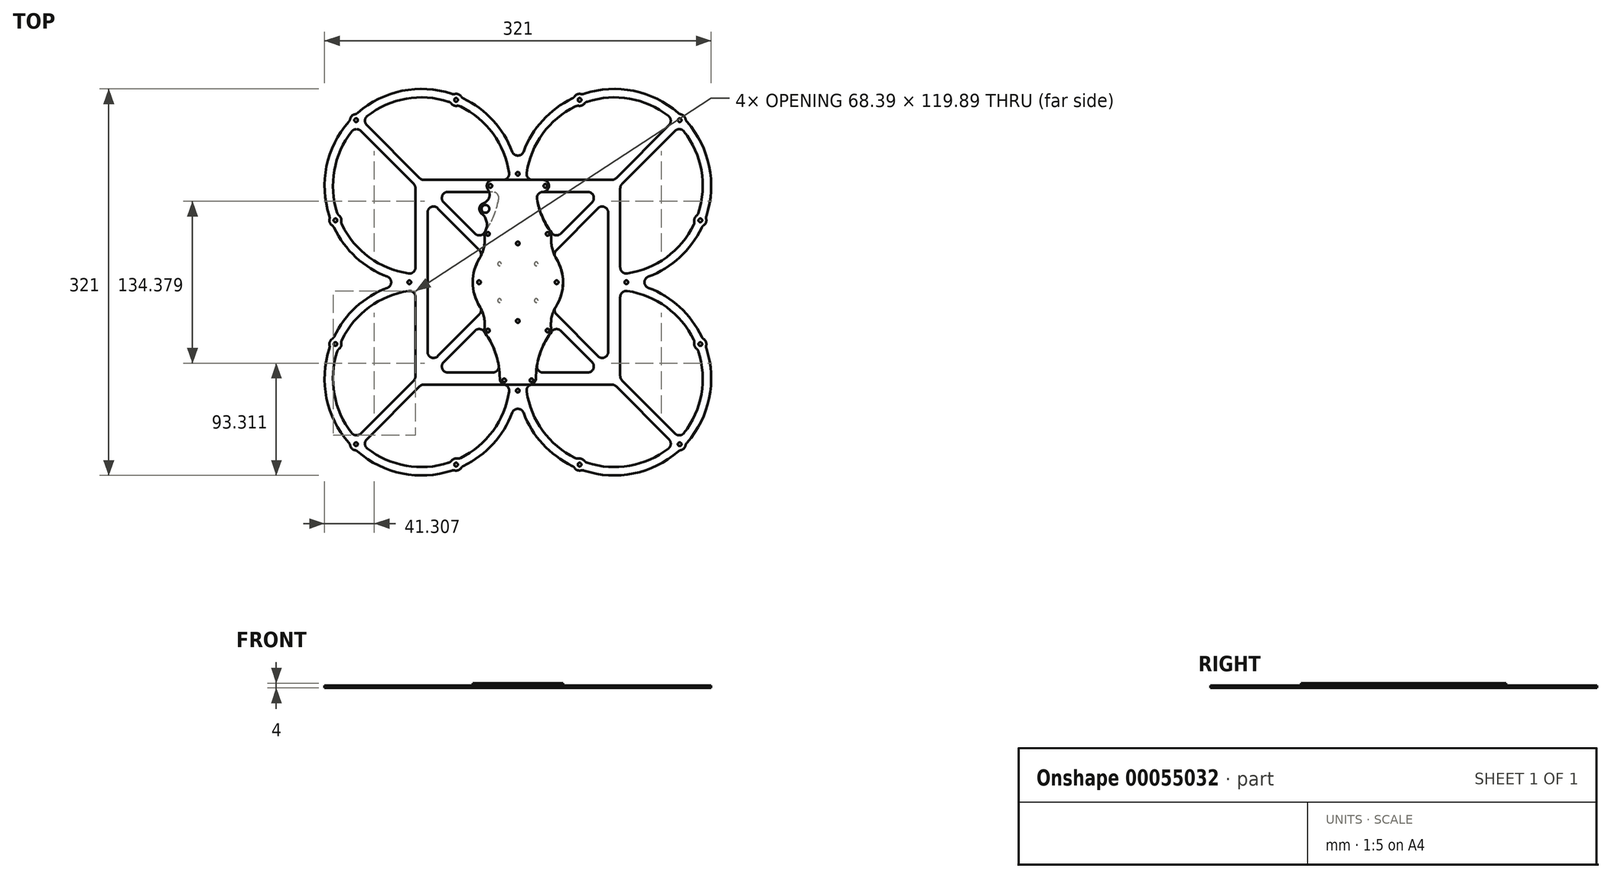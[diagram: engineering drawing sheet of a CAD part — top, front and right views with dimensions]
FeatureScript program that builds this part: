
annotation { "Feature Type Name" : "Feature", "Feature Type Description" : "" }
export const myFeature = defineFeature(function(context is Context, id is Id, definition is map)
    precondition{}
    {
        {
            var Q0;
            Q0=qCreatedBy(makeId("Top.planeOp"),FACE);
            var sketch = newSketch(context, id + "F0", { "sketchPlane" : qUnion([Q0])});
            skPoint(sketch, "E0.rect.middle", {"position": v(0, 0) * mm});
            skArc(sketch, "E1", {"start": v(80, -66) * mm, "mid": v(79.97, -66) * mm, "end": v(79.94, -66) * mm});
            skLineSegment(sketch, "E2.rect.bottom", {"start": v(15.25, -15.25) * mm, "end": v(-15.25, -15.25) * mm, "construction": true});
            skLineSegment(sketch, "E2.rect.top", {"start": v(15.25, 15.25) * mm, "end": v(-15.25, 15.25) * mm, "construction": true});
            skLineSegment(sketch, "E2.rect.left", {"start": v(15.25, -15.25) * mm, "end": v(15.25, 15.25) * mm, "construction": true});
            skLineSegment(sketch, "E2.rect.right", {"start": v(-15.25, -15.25) * mm, "end": v(-15.25, 15.25) * mm, "construction": true});
            skCircle(sketch, "E3", {"center": v(-80, 80) * mm, "radius": 63.5 * mm, "construction": true});
            skCircle(sketch, "E4", {"center": v(80, 80) * mm, "radius": 63.5 * mm, "construction": true});
            skCircle(sketch, "E5", {"center": v(-80, -80) * mm, "radius": 63.5 * mm, "construction": true});
            skCircle(sketch, "E6", {"center": v(80, -80) * mm, "radius": 63.5 * mm, "construction": true});
            skLineSegment(sketch, "E7.rect.bottom", {"start": v(26, -26) * mm, "end": v(-26, -26) * mm});
            skLineSegment(sketch, "E7.rect.top", {"start": v(26, 26) * mm, "end": v(-26, 26) * mm});
            skLineSegment(sketch, "E7.rect.left", {"start": v(26, -26) * mm, "end": v(26, 26) * mm});
            skLineSegment(sketch, "E7.rect.right", {"start": v(-26, -26) * mm, "end": v(-26, 26) * mm});
            skLineSegment(sketch, "E8.0", {"start": v(-85, -63.84) * mm, "end": v(-85, -12.23) * mm});
            skLineSegment(sketch, "E8.1", {"start": v(63.84, -85) * mm, "end": v(12.23, -85) * mm});
            skLineSegment(sketch, "E8.2", {"start": v(85, -63.84) * mm, "end": v(85, -12.23) * mm});
            skLineSegment(sketch, "E8.3", {"start": v(63.84, 85) * mm, "end": v(12.23, 85) * mm});
            skLineSegment(sketch, "E9.0", {"start": v(51.3, 75) * mm, "end": v(20.84, 75) * mm});
            skLineSegment(sketch, "E9.1", {"start": v(75, -51.34) * mm, "end": v(75, 51.3) * mm});
            skLineSegment(sketch, "E9.2", {"start": v(51.3, -75) * mm, "end": v(20.84, -75) * mm});
            skLineSegment(sketch, "E9.3", {"start": v(-75, -51.3) * mm, "end": v(-75, 51.3) * mm});
            skPoint(sketch, "E10", {"position": v(0, -124.8) * mm});
            skPoint(sketch, "E11.orphan", {"position": v(0, 114.1) * mm});
            skLineSegment(sketch, "E12.trimOffspring", {"start": v(-85, 12.23) * mm, "end": v(-85, 63.84) * mm});
            skLineSegment(sketch, "E13.trimOffspring", {"start": v(85, 12.23) * mm, "end": v(85, 63.84) * mm});
            skLineSegment(sketch, "E14.trimOffspring", {"start": v(-12.23, -85) * mm, "end": v(-63.84, -85) * mm});
            skLineSegment(sketch, "E15.trimOffspring", {"start": v(-12.23, 85) * mm, "end": v(-63.84, 85) * mm});
            skLineSegment(sketch, "E16", {"start": v(-124.66, 124.8) * mm, "end": v(-125, 125.15) * mm, "construction": true});
            skLineSegment(sketch, "E17", {"start": v(124.66, 124.8) * mm, "end": v(124.83, 124.97) * mm, "construction": true});
            skLineSegment(sketch, "E18", {"start": v(124.66, -124.8) * mm, "end": v(124.83, -124.97) * mm, "construction": true});
            skLineSegment(sketch, "E19", {"start": v(-124.66, -124.8) * mm, "end": v(-124.83, -124.97) * mm, "construction": true});
            skLineSegment(sketch, "E20.0", {"start": v(-94.48, 89.54) * mm, "end": v(-130.46, 125.67) * mm});
            skLineSegment(sketch, "E21.0", {"start": v(94.48, 89.54) * mm, "end": v(130.46, 125.67) * mm});
            skLineSegment(sketch, "E22.0", {"start": v(89.54, -94.5) * mm, "end": v(125.5, -130.61) * mm});
            skLineSegment(sketch, "E23.0", {"start": v(-94.48, -89.54) * mm, "end": v(-130.46, -125.67) * mm});
            skLineSegment(sketch, "E24.0", {"start": v(-89.54, 94.5) * mm, "end": v(-125.5, 130.61) * mm});
            skLineSegment(sketch, "E25.0", {"start": v(89.54, 94.5) * mm, "end": v(125.5, 130.61) * mm});
            skLineSegment(sketch, "E26.0", {"start": v(94.48, -89.54) * mm, "end": v(130.46, -125.67) * mm});
            skLineSegment(sketch, "E27.0", {"start": v(-89.54, -94.5) * mm, "end": v(-125.5, -130.61) * mm});
            skPoint(sketch, "E28.orphan", {"position": v(-89.9, 89.9) * mm});
            skPoint(sketch, "E29.orphan", {"position": v(-133.3, 133.48) * mm});
            skPoint(sketch, "E30.orphan", {"position": v(89.9, 89.9) * mm});
            skPoint(sketch, "E31.orphan", {"position": v(131.88, 132.06) * mm});
            skPoint(sketch, "E32.orphan", {"position": v(89.9, -89.9) * mm});
            skPoint(sketch, "E33.orphan", {"position": v(131.88, -132.06) * mm});
            skPoint(sketch, "E34.orphan", {"position": v(-89.9, -89.9) * mm});
            skPoint(sketch, "E35.orphan", {"position": v(-131.88, -132.06) * mm});
            skLineSegment(sketch, "E36", {"start": v(-87.42, 92.37) * mm, "end": v(-87.11, 92.06) * mm});
            skLineSegment(sketch, "E37", {"start": v(-92.38, 87.43) * mm, "end": v(-92.06, 87.1) * mm});
            skLineSegment(sketch, "E38", {"start": v(87.42, 92.37) * mm, "end": v(87.11, 92.06) * mm});
            skLineSegment(sketch, "E39", {"start": v(92.38, 87.43) * mm, "end": v(92.06, 87.1) * mm});
            skLineSegment(sketch, "E40", {"start": v(92.38, -87.43) * mm, "end": v(92.06, -87.1) * mm});
            skLineSegment(sketch, "E41", {"start": v(87.42, -92.37) * mm, "end": v(87.11, -92.06) * mm});
            skLineSegment(sketch, "E42", {"start": v(-92.38, -87.43) * mm, "end": v(-92.06, -87.1) * mm});
            skLineSegment(sketch, "E43", {"start": v(-87.42, -92.37) * mm, "end": v(-87.11, -92.06) * mm});
            skPoint(sketch, "E44.visualSharp", {"position": v(-66.92, 85) * mm});
            skPoint(sketch, "E45.visualSharp", {"position": v(-85, 66.92) * mm});
            skPoint(sketch, "E46.visualSharp", {"position": v(-61.92, 75) * mm});
            skPoint(sketch, "E47.visualSharp", {"position": v(-75, 61.92) * mm});
            skArc(sketch, "E48.filletArc", {"start": v(-125.02, 138.1) * mm, "mid": v(-126.95, 134.46) * mm, "end": v(-125.5, 130.61) * mm});
            skArc(sketch, "E49.filletArc", {"start": v(-130.46, 125.67) * mm, "mid": v(-134.3, 127.13) * mm, "end": v(-137.94, 125.22) * mm});
            skPoint(sketch, "E50.visualSharp", {"position": v(-4.93, 114.55) * mm});
            skPoint(sketch, "E51.visualSharp", {"position": v(5, 114.56) * mm});
            skPoint(sketch, "E52.visualSharp", {"position": v(66.92, 85) * mm});
            skArc(sketch, "E53.filletArc", {"start": v(125.5, 130.61) * mm, "mid": v(126.95, 134.46) * mm, "end": v(125.02, 138.1) * mm});
            skArc(sketch, "E54.filletArc", {"start": v(137.94, 125.22) * mm, "mid": v(134.3, 127.13) * mm, "end": v(130.46, 125.67) * mm});
            skPoint(sketch, "E55.visualSharp", {"position": v(85, 66.92) * mm});
            skPoint(sketch, "E56.visualSharp", {"position": v(61.92, 75) * mm});
            skPoint(sketch, "E57.visualSharp", {"position": v(75, 61.92) * mm});
            skLineSegment(sketch, "E57.filletArc", {"start": v(75, 51.3) * mm, "end": v(75, 51.3) * mm});
            skPoint(sketch, "E58.visualSharp", {"position": v(85, -66.92) * mm});
            skArc(sketch, "E59.filletArc", {"start": v(130.46, -125.67) * mm, "mid": v(134.3, -127.13) * mm, "end": v(137.94, -125.22) * mm});
            skArc(sketch, "E60.filletArc", {"start": v(125.02, -138.1) * mm, "mid": v(126.95, -134.46) * mm, "end": v(125.5, -130.61) * mm});
            skPoint(sketch, "E61.visualSharp", {"position": v(66.92, -85) * mm});
            skPoint(sketch, "E62.visualSharp", {"position": v(61.92, -75) * mm});
            skPoint(sketch, "E63.visualSharp", {"position": v(75, -61.96) * mm});
            skPoint(sketch, "E64.visualSharp", {"position": v(-5.02, -114.56) * mm});
            skPoint(sketch, "E65.visualSharp", {"position": v(-66.92, -85) * mm});
            skArc(sketch, "E66.filletArc", {"start": v(-125.5, -130.61) * mm, "mid": v(-126.95, -134.46) * mm, "end": v(-125.02, -138.1) * mm});
            skArc(sketch, "E67.filletArc", {"start": v(-137.94, -125.22) * mm, "mid": v(-134.3, -127.13) * mm, "end": v(-130.46, -125.67) * mm});
            skPoint(sketch, "E68.visualSharp", {"position": v(-85, -66.92) * mm});
            skPoint(sketch, "E69.visualSharp", {"position": v(-61.92, -75) * mm});
            skPoint(sketch, "E70.visualSharp", {"position": v(-75, -61.92) * mm});
            skArc(sketch, "E71", {"start": v(33.54, -16.78) * mm, "mid": v(37.5, 0) * mm, "end": v(33.54, 16.77) * mm});
            skArc(sketch, "E72.trimOffspring", {"start": v(-33.54, 16.77) * mm, "mid": v(-37.5, 0) * mm, "end": v(-33.54, -16.77) * mm});
            skPoint(sketch, "E73.visualSharp", {"position": v(-19.22, 32.2) * mm});
            skPoint(sketch, "E74.visualSharp", {"position": v(19.22, 32.2) * mm});
            skPoint(sketch, "E75.visualSharp", {"position": v(32.2, 19.22) * mm});
            skPoint(sketch, "E76.visualSharp", {"position": v(32.2, -19.23) * mm});
            skPoint(sketch, "E77.visualSharp", {"position": v(-32.2, -19.22) * mm});
            skPoint(sketch, "E78.visualSharp", {"position": v(-32.2, 19.22) * mm});
            skCircle(sketch, "E79", {"center": v(15.25, -15.25) * mm, "radius": 1.5 * mm});
            skCircle(sketch, "E80", {"center": v(-15.25, -15.25) * mm, "radius": 1.5 * mm});
            skCircle(sketch, "E81", {"center": v(-15.25, 15.25) * mm, "radius": 1.5 * mm});
            skCircle(sketch, "E82", {"center": v(15.25, 15.25) * mm, "radius": 1.5 * mm});
            skCircle(sketch, "E83", {"center": v(32.2, 0) * mm, "radius": 1.5 * mm});
            skCircle(sketch, "E84", {"center": v(0, -32.2) * mm, "radius": 1.5 * mm});
            skLineSegment(sketch, "E85", {"start": v(0, -141.51) * mm, "end": v(0, 75) * mm, "construction": true});
            skLineSegment(sketch, "E86", {"start": v(141.95, 0) * mm, "end": v(-75, 0) * mm, "construction": true});
            skCircle(sketch, "E87.MirrorC", {"center": v(-32.2, 0) * mm, "radius": 1.5 * mm});
            skCircle(sketch, "E88.MirrorC", {"center": v(0, 32.2) * mm, "radius": 1.5 * mm});
            skArc(sketch, "E89.filletArc", {"start": v(12.23, -85) * mm, "mid": v(8.45, -86.73) * mm, "end": v(7.29, -90.73) * mm});
            skArc(sketch, "E90.filletArc", {"start": v(-7.29, -90.73) * mm, "mid": v(-8.45, -86.73) * mm, "end": v(-12.23, -85) * mm});
            skArc(sketch, "E91.filletArc", {"start": v(4.68, -108.4) * mm, "mid": v(0, -105.17) * mm, "end": v(-4.68, -108.4) * mm});
            skPoint(sketch, "E92.visualSharp", {"position": v(6.67, 85) * mm});
            skArc(sketch, "E92.filletArc", {"start": v(7.29, 90.73) * mm, "mid": v(8.45, 86.73) * mm, "end": v(12.23, 85) * mm});
            skPoint(sketch, "E93.visualSharp", {"position": v(-6.67, 85) * mm});
            skArc(sketch, "E93.filletArc", {"start": v(-12.23, 85) * mm, "mid": v(-8.45, 86.73) * mm, "end": v(-7.29, 90.73) * mm});
            skPoint(sketch, "E94.visualSharp", {"position": v(0, 88.96) * mm});
            skArc(sketch, "E94.filletArc", {"start": v(-4.68, 108.4) * mm, "mid": v(0, 105.17) * mm, "end": v(4.68, 108.4) * mm});
            skArc(sketch, "E95.filletArc", {"start": v(-85, -12.23) * mm, "mid": v(-86.73, -8.45) * mm, "end": v(-90.73, -7.29) * mm});
            skArc(sketch, "E96.filletArc", {"start": v(-90.73, 7.29) * mm, "mid": v(-86.73, 8.45) * mm, "end": v(-85, 12.23) * mm});
            skPoint(sketch, "E97.visualSharp", {"position": v(-88.96, 0) * mm});
            skArc(sketch, "E97.filletArc", {"start": v(-108.4, -4.68) * mm, "mid": v(-105.17, 0) * mm, "end": v(-108.4, 4.68) * mm});
            skPoint(sketch, "E98.visualSharp", {"position": v(85, -6.67) * mm});
            skArc(sketch, "E98.filletArc", {"start": v(90.73, -7.29) * mm, "mid": v(86.73, -8.45) * mm, "end": v(85, -12.23) * mm});
            skPoint(sketch, "E99.visualSharp", {"position": v(85, 6.67) * mm});
            skArc(sketch, "E99.filletArc", {"start": v(85, 12.23) * mm, "mid": v(86.73, 8.45) * mm, "end": v(90.73, 7.29) * mm});
            skArc(sketch, "E100.filletArc", {"start": v(108.4, 4.68) * mm, "mid": v(105.17, 0) * mm, "end": v(108.4, -4.68) * mm});
            skArc(sketch, "E101", {"start": v(-90.73, 7.29) * mm, "mid": v(-123.42, 20.7) * mm, "end": v(-146.07, 47.8) * mm});
            skArc(sketch, "E102", {"start": v(-108.4, 4.68) * mm, "mid": v(-134.45, 20.7) * mm, "end": v(-152.63, 45.3) * mm});
            skArc(sketch, "E103", {"start": v(-7.29, 90.73) * mm, "mid": v(-20.66, 123.37) * mm, "end": v(-47.7, 146.02) * mm});
            skLineSegment(sketch, "E104", {"start": v(-138.95, 56.4) * mm, "end": v(-148.23, 52.68) * mm, "construction": true});
            skLineSegment(sketch, "E105", {"start": v(-148.23, 52.68) * mm, "end": v(-160.6, 47.73) * mm, "construction": true});
            skLineSegment(sketch, "E106", {"start": v(-52.57, 148.19) * mm, "end": v(-48.09, 159.32) * mm, "construction": true});
            skCircle(sketch, "E107", {"center": v(-80, 80) * mm, "radius": 77 * mm, "construction": true});
            skArc(sketch, "E108", {"start": v(-156.38, 52.4) * mm, "mid": v(-156.13, 49.52) * mm, "end": v(-154.31, 47.26) * mm});
            skArc(sketch, "E109", {"start": v(-55.18, 148.34) * mm, "mid": v(-53.13, 146.8) * mm, "end": v(-50.58, 146.48) * mm});
            skArc(sketch, "E110.trimOffspring", {"start": v(-47.14, 154.26) * mm, "mid": v(-49.4, 156.07) * mm, "end": v(-52.28, 156.33) * mm});
            skArc(sketch, "E111.trimOffspring", {"start": v(-45.17, 152.58) * mm, "mid": v(-20.66, 134.4) * mm, "end": v(-4.68, 108.4) * mm});
            skArc(sketch, "E112.trimOffspring", {"start": v(-57.58, 150) * mm, "mid": v(-92.77, 152.38) * mm, "end": v(-125.02, 138.1) * mm});
            skPoint(sketch, "E113.visualSharp", {"position": v(-46.6, 153.24) * mm});
            skArc(sketch, "E113.filletArc", {"start": v(-47.14, 154.26) * mm, "mid": v(-46.26, 153.29) * mm, "end": v(-45.17, 152.58) * mm});
            skPoint(sketch, "E114.visualSharp", {"position": v(-49.36, 146.81) * mm});
            skArc(sketch, "E114.filletArc", {"start": v(-47.7, 146.02) * mm, "mid": v(-49.1, 146.47) * mm, "end": v(-50.58, 146.48) * mm});
            skPoint(sketch, "E115.visualSharp", {"position": v(-55.83, 149.41) * mm});
            skArc(sketch, "E115.filletArc", {"start": v(-55.18, 148.34) * mm, "mid": v(-56.26, 149.35) * mm, "end": v(-57.58, 150) * mm});
            skPoint(sketch, "E116.visualSharp", {"position": v(-53.37, 155.97) * mm});
            skArc(sketch, "E116.filletArc", {"start": v(-54.86, 156.48) * mm, "mid": v(-53.58, 156.23) * mm, "end": v(-52.28, 156.33) * mm});
            skArc(sketch, "E117.trimOffspring", {"start": v(-156.52, 55) * mm, "mid": v(-158.84, 96.26) * mm, "end": v(-140.38, 133.24) * mm});
            skArc(sketch, "E118.trimOffspring", {"start": v(-150.04, 57.7) * mm, "mid": v(-152.35, 92.96) * mm, "end": v(-137.94, 125.22) * mm});
            skArc(sketch, "E119.trimOffspring", {"start": v(-146.53, 50.69) * mm, "mid": v(-146.84, 53.24) * mm, "end": v(-148.38, 55.3) * mm});
            skPoint(sketch, "E120.visualSharp", {"position": v(-153.3, 46.72) * mm});
            skArc(sketch, "E120.filletArc", {"start": v(-152.63, 45.3) * mm, "mid": v(-153.35, 46.39) * mm, "end": v(-154.31, 47.26) * mm});
            skPoint(sketch, "E121.visualSharp", {"position": v(-146.86, 49.47) * mm});
            skArc(sketch, "E121.filletArc", {"start": v(-146.53, 50.69) * mm, "mid": v(-146.52, 49.21) * mm, "end": v(-146.07, 47.8) * mm});
            skPoint(sketch, "E122.visualSharp", {"position": v(-149.45, 55.95) * mm});
            skArc(sketch, "E122.filletArc", {"start": v(-150.04, 57.7) * mm, "mid": v(-149.39, 56.38) * mm, "end": v(-148.38, 55.3) * mm});
            skPoint(sketch, "E123.visualSharp", {"position": v(-156.01, 53.5) * mm});
            skArc(sketch, "E123.filletArc", {"start": v(-156.38, 52.4) * mm, "mid": v(-156.28, 53.71) * mm, "end": v(-156.52, 55) * mm});
            skCircle(sketch, "E124", {"center": v(-151.48, 51.38) * mm, "radius": 1.5 * mm});
            skCircle(sketch, "E125", {"center": v(-51.26, 151.44) * mm, "radius": 1.5 * mm});
            skArc(sketch, "E126", {"start": v(7.29, 90.73) * mm, "mid": v(20.66, 123.37) * mm, "end": v(47.7, 146.02) * mm});
            skArc(sketch, "E127", {"start": v(137.94, 125.22) * mm, "mid": v(152.35, 92.96) * mm, "end": v(150.04, 57.7) * mm});
            skArc(sketch, "E128", {"start": v(4.68, 108.4) * mm, "mid": v(20.66, 134.4) * mm, "end": v(45.17, 152.58) * mm});
            skArc(sketch, "E129", {"start": v(90.73, -7.29) * mm, "mid": v(123.42, -20.7) * mm, "end": v(146.07, -47.8) * mm});
            skArc(sketch, "E130", {"start": v(125.02, -138.1) * mm, "mid": v(92.77, -152.38) * mm, "end": v(57.58, -150) * mm});
            skArc(sketch, "E131", {"start": v(108.4, -4.68) * mm, "mid": v(134.45, -20.7) * mm, "end": v(152.63, -45.3) * mm});
            skArc(sketch, "E132", {"start": v(-90.73, -7.29) * mm, "mid": v(-123.42, -20.7) * mm, "end": v(-146.07, -47.8) * mm});
            skArc(sketch, "E133", {"start": v(-125.02, -138.1) * mm, "mid": v(-92.77, -152.38) * mm, "end": v(-57.58, -150) * mm});
            skArc(sketch, "E134", {"start": v(-108.4, -4.68) * mm, "mid": v(-134.45, -20.7) * mm, "end": v(-152.63, -45.3) * mm});
            skArc(sketch, "E135.MirrorCS", {"start": v(47.14, 154.26) * mm, "mid": v(49.4, 156.07) * mm, "end": v(52.28, 156.33) * mm});
            skArc(sketch, "E136.MirrorCS", {"start": v(55.18, 148.34) * mm, "mid": v(53.13, 146.8) * mm, "end": v(50.58, 146.48) * mm});
            skCircle(sketch, "E137.MirrorC", {"center": v(51.26, 151.44) * mm, "radius": 1.5 * mm});
            skArc(sketch, "E138.MirrorCS", {"start": v(55.18, 148.34) * mm, "mid": v(56.26, 149.35) * mm, "end": v(57.58, 150) * mm});
            skArc(sketch, "E139.MirrorCS", {"start": v(47.7, 146.02) * mm, "mid": v(49.1, 146.47) * mm, "end": v(50.58, 146.48) * mm});
            skArc(sketch, "E140.MirrorCS", {"start": v(47.14, 154.26) * mm, "mid": v(46.26, 153.29) * mm, "end": v(45.17, 152.58) * mm});
            skArc(sketch, "E141.MirrorCS", {"start": v(54.86, 156.48) * mm, "mid": v(53.58, 156.23) * mm, "end": v(52.28, 156.33) * mm});
            skCircle(sketch, "E142.MirrorC", {"center": v(151.48, 51.38) * mm, "radius": 1.5 * mm});
            skArc(sketch, "E143.MirrorCS", {"start": v(146.53, 50.69) * mm, "mid": v(146.84, 53.24) * mm, "end": v(148.38, 55.3) * mm});
            skArc(sketch, "E144.MirrorCS", {"start": v(156.38, 52.4) * mm, "mid": v(156.13, 49.52) * mm, "end": v(154.31, 47.26) * mm});
            skArc(sketch, "E145.MirrorCS", {"start": v(156.38, 52.4) * mm, "mid": v(156.28, 53.71) * mm, "end": v(156.52, 55) * mm});
            skArc(sketch, "E146.MirrorCS", {"start": v(150.04, 57.7) * mm, "mid": v(149.39, 56.38) * mm, "end": v(148.38, 55.3) * mm});
            skArc(sketch, "E147.MirrorCS", {"start": v(146.53, 50.69) * mm, "mid": v(146.52, 49.21) * mm, "end": v(146.07, 47.8) * mm});
            skArc(sketch, "E148.MirrorCS", {"start": v(152.63, 45.3) * mm, "mid": v(153.35, 46.39) * mm, "end": v(154.31, 47.26) * mm});
            skLineSegment(sketch, "E149", {"start": v(-80, 80) * mm, "end": v(-139.42, 139.67) * mm, "construction": true});
            skArc(sketch, "E150", {"start": v(-135.3, 139.47) * mm, "mid": v(-137.86, 138.1) * mm, "end": v(-139.23, 135.55) * mm});
            skCircle(sketch, "E151", {"center": v(-134.33, 134.56) * mm, "radius": 1.5 * mm});
            skArc(sketch, "E152.trimOffspring", {"start": v(-132.98, 140.6) * mm, "mid": v(-96.03, 158.89) * mm, "end": v(-54.86, 156.48) * mm});
            skPoint(sketch, "E153.visualSharp", {"position": v(-139.33, 134.4) * mm});
            skArc(sketch, "E153.filletArc", {"start": v(-140.38, 133.24) * mm, "mid": v(-139.66, 134.32) * mm, "end": v(-139.23, 135.55) * mm});
            skPoint(sketch, "E154.visualSharp", {"position": v(-134.16, 139.56) * mm});
            skArc(sketch, "E154.filletArc", {"start": v(-135.3, 139.47) * mm, "mid": v(-134.07, 139.88) * mm, "end": v(-132.98, 140.6) * mm});
            skCircle(sketch, "E155.MirrorC", {"center": v(134.33, 134.56) * mm, "radius": 1.5 * mm});
            skArc(sketch, "E156.MirrorCS", {"start": v(135.3, 139.47) * mm, "mid": v(137.86, 138.1) * mm, "end": v(139.23, 135.55) * mm});
            skArc(sketch, "E157.MirrorCS", {"start": v(135.3, 139.47) * mm, "mid": v(134.07, 139.88) * mm, "end": v(132.98, 140.6) * mm});
            skArc(sketch, "E158.MirrorCS", {"start": v(140.38, 133.24) * mm, "mid": v(139.66, 134.32) * mm, "end": v(139.23, 135.55) * mm});
            skArc(sketch, "E159.trimOffspring", {"start": v(54.86, 156.48) * mm, "mid": v(96.03, 158.89) * mm, "end": v(132.98, 140.6) * mm});
            skArc(sketch, "E160.trimOffspring", {"start": v(57.58, 150) * mm, "mid": v(92.77, 152.38) * mm, "end": v(125.02, 138.1) * mm});
            skArc(sketch, "E161.trimOffspring", {"start": v(140.38, 133.24) * mm, "mid": v(158.84, 96.26) * mm, "end": v(156.52, 55) * mm});
            skArc(sketch, "E162.trimOffspring", {"start": v(146.07, 47.8) * mm, "mid": v(123.42, 20.7) * mm, "end": v(90.73, 7.29) * mm});
            skArc(sketch, "E163.trimOffspring", {"start": v(152.63, 45.3) * mm, "mid": v(134.45, 20.7) * mm, "end": v(108.4, 4.68) * mm});
            skArc(sketch, "E164.MirrorCS", {"start": v(-156.38, -52.4) * mm, "mid": v(-156.28, -53.71) * mm, "end": v(-156.52, -55) * mm});
            skArc(sketch, "E165.MirrorCS", {"start": v(-156.38, -52.4) * mm, "mid": v(-156.13, -49.52) * mm, "end": v(-154.31, -47.26) * mm});
            skArc(sketch, "E166.MirrorCS", {"start": v(-152.63, -45.3) * mm, "mid": v(-153.35, -46.39) * mm, "end": v(-154.31, -47.26) * mm});
            skArc(sketch, "E167.MirrorCS", {"start": v(-150.04, -57.7) * mm, "mid": v(-149.39, -56.38) * mm, "end": v(-148.38, -55.3) * mm});
            skArc(sketch, "E168.MirrorCS", {"start": v(-146.53, -50.69) * mm, "mid": v(-146.84, -53.24) * mm, "end": v(-148.38, -55.3) * mm});
            skArc(sketch, "E169.MirrorCS", {"start": v(-146.53, -50.69) * mm, "mid": v(-146.52, -49.21) * mm, "end": v(-146.07, -47.8) * mm});
            skArc(sketch, "E170.MirrorCS", {"start": v(-135.3, -139.47) * mm, "mid": v(-137.86, -138.1) * mm, "end": v(-139.23, -135.55) * mm});
            skArc(sketch, "E171.MirrorCS", {"start": v(-135.3, -139.47) * mm, "mid": v(-134.07, -139.88) * mm, "end": v(-132.98, -140.6) * mm});
            skArc(sketch, "E172.MirrorCS", {"start": v(-140.38, -133.24) * mm, "mid": v(-139.66, -134.32) * mm, "end": v(-139.23, -135.55) * mm});
            skArc(sketch, "E173.MirrorCS", {"start": v(-54.86, -156.48) * mm, "mid": v(-53.58, -156.23) * mm, "end": v(-52.28, -156.33) * mm});
            skArc(sketch, "E174.MirrorCS", {"start": v(-47.14, -154.26) * mm, "mid": v(-49.4, -156.07) * mm, "end": v(-52.28, -156.33) * mm});
            skArc(sketch, "E175.MirrorCS", {"start": v(-47.7, -146.02) * mm, "mid": v(-49.1, -146.47) * mm, "end": v(-50.58, -146.48) * mm});
            skArc(sketch, "E176.MirrorCS", {"start": v(-55.18, -148.34) * mm, "mid": v(-53.13, -146.8) * mm, "end": v(-50.58, -146.48) * mm});
            skArc(sketch, "E177.MirrorCS", {"start": v(-55.18, -148.34) * mm, "mid": v(-56.26, -149.35) * mm, "end": v(-57.58, -150) * mm});
            skArc(sketch, "E178.MirrorCS", {"start": v(47.14, -154.26) * mm, "mid": v(46.26, -153.29) * mm, "end": v(45.17, -152.58) * mm});
            skArc(sketch, "E179.MirrorCS", {"start": v(47.14, -154.26) * mm, "mid": v(49.4, -156.07) * mm, "end": v(52.28, -156.33) * mm});
            skArc(sketch, "E180.MirrorCS", {"start": v(54.86, -156.48) * mm, "mid": v(53.58, -156.23) * mm, "end": v(52.28, -156.33) * mm});
            skArc(sketch, "E181.MirrorCS", {"start": v(55.18, -148.34) * mm, "mid": v(56.26, -149.35) * mm, "end": v(57.58, -150) * mm});
            skArc(sketch, "E182.MirrorCS", {"start": v(55.18, -148.34) * mm, "mid": v(53.13, -146.8) * mm, "end": v(50.58, -146.48) * mm});
            skArc(sketch, "E183.MirrorCS", {"start": v(47.7, -146.02) * mm, "mid": v(49.1, -146.47) * mm, "end": v(50.58, -146.48) * mm});
            skCircle(sketch, "E184.MirrorC", {"center": v(51.26, -151.44) * mm, "radius": 1.5 * mm});
            skCircle(sketch, "E185.MirrorC", {"center": v(-51.26, -151.44) * mm, "radius": 1.5 * mm});
            skCircle(sketch, "E186.MirrorC", {"center": v(-134.33, -134.56) * mm, "radius": 1.5 * mm});
            skCircle(sketch, "E187.MirrorC", {"center": v(-151.48, -51.38) * mm, "radius": 1.5 * mm});
            skCircle(sketch, "E188.MirrorC", {"center": v(151.48, -51.38) * mm, "radius": 1.5 * mm});
            skArc(sketch, "E189.MirrorCS", {"start": v(150.04, -57.7) * mm, "mid": v(149.39, -56.38) * mm, "end": v(148.38, -55.3) * mm});
            skArc(sketch, "E190.MirrorCS", {"start": v(146.53, -50.69) * mm, "mid": v(146.84, -53.24) * mm, "end": v(148.38, -55.3) * mm});
            skArc(sketch, "E191.MirrorCS", {"start": v(146.53, -50.69) * mm, "mid": v(146.52, -49.21) * mm, "end": v(146.07, -47.8) * mm});
            skArc(sketch, "E192.MirrorCS", {"start": v(156.38, -52.4) * mm, "mid": v(156.28, -53.71) * mm, "end": v(156.52, -55) * mm});
            skArc(sketch, "E193.MirrorCS", {"start": v(156.38, -52.4) * mm, "mid": v(156.13, -49.52) * mm, "end": v(154.31, -47.26) * mm});
            skArc(sketch, "E194.MirrorCS", {"start": v(152.63, -45.3) * mm, "mid": v(153.35, -46.39) * mm, "end": v(154.31, -47.26) * mm});
            skCircle(sketch, "E195.MirrorC", {"center": v(134.33, -134.56) * mm, "radius": 1.5 * mm});
            skArc(sketch, "E196.MirrorCS", {"start": v(135.3, -139.47) * mm, "mid": v(134.07, -139.88) * mm, "end": v(132.98, -140.6) * mm});
            skArc(sketch, "E197.MirrorCS", {"start": v(135.3, -139.47) * mm, "mid": v(137.86, -138.1) * mm, "end": v(139.23, -135.55) * mm});
            skArc(sketch, "E198.MirrorCS", {"start": v(140.38, -133.24) * mm, "mid": v(139.66, -134.32) * mm, "end": v(139.23, -135.55) * mm});
            skArc(sketch, "E199.trimOffspring", {"start": v(150.04, -57.7) * mm, "mid": v(152.35, -92.96) * mm, "end": v(137.94, -125.22) * mm});
            skArc(sketch, "E200.trimOffspring", {"start": v(156.52, -55) * mm, "mid": v(158.84, -96.26) * mm, "end": v(140.38, -133.24) * mm});
            skArc(sketch, "E201.trimOffspring", {"start": v(132.98, -140.6) * mm, "mid": v(96.03, -158.89) * mm, "end": v(54.86, -156.48) * mm});
            skArc(sketch, "E202.trimOffspring", {"start": v(45.17, -152.58) * mm, "mid": v(20.66, -134.4) * mm, "end": v(4.68, -108.4) * mm});
            skArc(sketch, "E203.trimOffspring", {"start": v(47.7, -146.02) * mm, "mid": v(20.66, -123.37) * mm, "end": v(7.29, -90.73) * mm});
            skArc(sketch, "E204.trimOffspring", {"start": v(-47.7, -146.02) * mm, "mid": v(-20.66, -123.37) * mm, "end": v(-7.29, -90.73) * mm});
            skArc(sketch, "E205.MirrorCS", {"start": v(-47.14, -154.26) * mm, "mid": v(-46.26, -153.29) * mm, "end": v(-45.17, -152.58) * mm});
            skArc(sketch, "E206.trimOffspring", {"start": v(-45.17, -152.58) * mm, "mid": v(-20.66, -134.4) * mm, "end": v(-4.68, -108.4) * mm});
            skArc(sketch, "E207.trimOffspring", {"start": v(-132.98, -140.6) * mm, "mid": v(-96.03, -158.89) * mm, "end": v(-54.86, -156.48) * mm});
            skArc(sketch, "E208.trimOffspring", {"start": v(-156.52, -55) * mm, "mid": v(-158.84, -96.26) * mm, "end": v(-140.38, -133.24) * mm});
            skArc(sketch, "E209.trimOffspring", {"start": v(-150.04, -57.7) * mm, "mid": v(-152.35, -92.96) * mm, "end": v(-137.94, -125.22) * mm});
            skLineSegment(sketch, "E210.trimOffspring", {"start": v(-75, 0) * mm, "end": v(141.95, 0) * mm, "construction": true});
            skPoint(sketch, "E211.MirrorCS.start.orphan", {"position": v(-141.95, 0) * mm});
            skLineSegment(sketch, "E212.trimOffspring", {"start": v(-105.17, 0) * mm, "end": v(-110.17, 0) * mm, "construction": true});
            skCircle(sketch, "E213", {"center": v(-90.09, 0) * mm, "radius": 1.5 * mm});
            skLineSegment(sketch, "E214.trimOffspring", {"start": v(0, 105.17) * mm, "end": v(0, 141.51) * mm, "construction": true});
            skCircle(sketch, "E215", {"center": v(0, 90.09) * mm, "radius": 1.5 * mm});
            skCircle(sketch, "E216.MirrorC", {"center": v(0, -90.09) * mm, "radius": 1.5 * mm});
            skCircle(sketch, "E217.MirrorC", {"center": v(90.09, 0) * mm, "radius": 1.5 * mm});
            skLineSegment(sketch, "E218.trimOffspring", {"start": v(-56.3, 138.91) * mm, "end": v(-52.57, 148.19) * mm, "construction": true});
            skArc(sketch, "E219", {"start": v(-31.37, 20.54) * mm, "mid": v(-37.5, 0) * mm, "end": v(-31.37, -20.54) * mm});
            skLineSegment(sketch, "E220", {"start": v(89.54, 94.5) * mm, "end": v(81.55, 86.47) * mm});
            skLineSegment(sketch, "E221", {"start": v(94.48, 89.54) * mm, "end": v(86.46, 81.48) * mm});
            skLineSegment(sketch, "E222", {"start": v(63.84, 85) * mm, "end": v(78, 85) * mm});
            skLineSegment(sketch, "E223", {"start": v(51.3, 75) * mm, "end": v(58.09, 75) * mm});
            skLineSegment(sketch, "E224", {"start": v(85, 63.84) * mm, "end": v(85, 77.95) * mm});
            skLineSegment(sketch, "E225", {"start": v(75, 51.3) * mm, "end": v(75, 57.87) * mm});
            skLineSegment(sketch, "E226", {"start": v(-89.54, 94.5) * mm, "end": v(-81.55, 86.47) * mm});
            skLineSegment(sketch, "E227", {"start": v(-94.48, 89.54) * mm, "end": v(-86.46, 81.48) * mm});
            skLineSegment(sketch, "E228", {"start": v(-63.84, 85) * mm, "end": v(-78, 85) * mm});
            skLineSegment(sketch, "E229", {"start": v(-51.3, 75) * mm, "end": v(-58.09, 75) * mm});
            skLineSegment(sketch, "E230", {"start": v(-75, 51.3) * mm, "end": v(-75, 57.87) * mm});
            skLineSegment(sketch, "E231", {"start": v(-85, 63.84) * mm, "end": v(-85, 77.95) * mm});
            skPoint(sketch, "E232.1.internal.orphan", {"position": v(-26, 0) * mm});
            skPoint(sketch, "E233.1.internal.orphan", {"position": v(0, 26) * mm});
            skArc(sketch, "E234", {"start": v(-15.9, 69.17) * mm, "mid": v(-20.3, 54.3) * mm, "end": v(-28.1, 40.88) * mm});
            skArc(sketch, "E235", {"start": v(15.9, 69.17) * mm, "mid": v(20.3, 54.3) * mm, "end": v(28.1, 40.88) * mm});
            skLineSegment(sketch, "E236", {"start": v(94.48, -89.54) * mm, "end": v(86.46, -81.48) * mm});
            skLineSegment(sketch, "E237", {"start": v(89.54, -94.5) * mm, "end": v(81.55, -86.47) * mm});
            skLineSegment(sketch, "E238", {"start": v(75, -51.34) * mm, "end": v(75, -57.87) * mm});
            skLineSegment(sketch, "E239", {"start": v(51.3, -75) * mm, "end": v(58.09, -75) * mm});
            skLineSegment(sketch, "E240", {"start": v(63.84, -85) * mm, "end": v(78, -85) * mm});
            skLineSegment(sketch, "E241", {"start": v(85, -63.84) * mm, "end": v(85, -77.95) * mm});
            skPoint(sketch, "E242.1.internal.orphan", {"position": v(26, 0) * mm});
            skLineSegment(sketch, "E243", {"start": v(-94.48, -89.54) * mm, "end": v(-86.46, -81.48) * mm});
            skLineSegment(sketch, "E244", {"start": v(-89.54, -94.5) * mm, "end": v(-81.55, -86.47) * mm});
            skLineSegment(sketch, "E245", {"start": v(-85, -63.84) * mm, "end": v(-85, -77.95) * mm});
            skLineSegment(sketch, "E246", {"start": v(-63.84, -85) * mm, "end": v(-78, -85) * mm});
            skLineSegment(sketch, "E247", {"start": v(-51.3, -75) * mm, "end": v(-58.09, -75) * mm});
            skLineSegment(sketch, "E248", {"start": v(-75, -51.3) * mm, "end": v(-75, -57.87) * mm});
            skPoint(sketch, "E249.1.internal.orphan", {"position": v(0, -26) * mm});
            skArc(sketch, "E250", {"start": v(28.1, -40.88) * mm, "mid": v(20.3, -54.3) * mm, "end": v(15.9, -69.17) * mm});
            skArc(sketch, "E251", {"start": v(-28.1, -40.88) * mm, "mid": v(-20.3, -54.3) * mm, "end": v(-15.9, -69.17) * mm});
            skLineSegment(sketch, "E252.trimOffspring", {"start": v(-61.63, 66.47) * mm, "end": v(-35.63, 40.36) * mm});
            skLineSegment(sketch, "E253.trimOffspring", {"start": v(-66.46, 61.4) * mm, "end": v(-32.01, 26.8) * mm});
            skLineSegment(sketch, "E254.trimOffspring", {"start": v(61.63, 66.47) * mm, "end": v(35.63, 40.36) * mm});
            skLineSegment(sketch, "E255.trimOffspring", {"start": v(66.46, 61.4) * mm, "end": v(32.01, 26.8) * mm});
            skLineSegment(sketch, "E256.trimOffspring", {"start": v(66.46, -61.4) * mm, "end": v(32.01, -26.8) * mm});
            skLineSegment(sketch, "E257.trimOffspring", {"start": v(61.63, -66.47) * mm, "end": v(35.63, -40.36) * mm});
            skLineSegment(sketch, "E258.trimOffspring", {"start": v(-61.63, -66.47) * mm, "end": v(-35.63, -40.36) * mm});
            skLineSegment(sketch, "E259.trimOffspring", {"start": v(-66.46, -61.4) * mm, "end": v(-32.01, -26.8) * mm});
            skPoint(sketch, "E260.visualSharp", {"position": v(-70.12, 75) * mm});
            skArc(sketch, "E260.filletArc", {"start": v(-58.09, 75) * mm, "mid": v(-62.7, 71.92) * mm, "end": v(-61.63, 66.47) * mm});
            skPoint(sketch, "E261.visualSharp", {"position": v(-75, 69.98) * mm});
            skArc(sketch, "E261.filletArc", {"start": v(-66.46, 61.4) * mm, "mid": v(-71.9, 62.5) * mm, "end": v(-75, 57.87) * mm});
            skPoint(sketch, "E262.visualSharp", {"position": v(70.12, 75) * mm});
            skArc(sketch, "E262.filletArc", {"start": v(61.63, 66.47) * mm, "mid": v(62.7, 71.92) * mm, "end": v(58.09, 75) * mm});
            skPoint(sketch, "E263.visualSharp", {"position": v(75, 69.98) * mm});
            skArc(sketch, "E263.filletArc", {"start": v(75, 57.87) * mm, "mid": v(71.9, 62.5) * mm, "end": v(66.46, 61.4) * mm});
            skArc(sketch, "E264.filletArc", {"start": v(28.1, 40.88) * mm, "mid": v(31.74, 38.9) * mm, "end": v(35.63, 40.36) * mm});
            skArc(sketch, "E265.filletArc", {"start": v(-35.63, 40.36) * mm, "mid": v(-31.74, 38.9) * mm, "end": v(-28.1, 40.88) * mm});
            skLineSegment(sketch, "E266.trimOffspring", {"start": v(-20.84, 75) * mm, "end": v(-51.3, 75) * mm});
            skPoint(sketch, "E267.visualSharp", {"position": v(-15.2, 75) * mm});
            skArc(sketch, "E267.filletArc", {"start": v(-15.9, 69.17) * mm, "mid": v(-17.02, 73.23) * mm, "end": v(-20.84, 75) * mm});
            skArc(sketch, "E268.filletArc", {"start": v(20.84, 75) * mm, "mid": v(17.02, 73.23) * mm, "end": v(15.9, 69.17) * mm});
            skArc(sketch, "E269.trimOffspring", {"start": v(-19.22, 32.2) * mm, "mid": v(-19.63, 31.95) * mm, "end": v(-20.03, 31.7) * mm});
            skPoint(sketch, "E270.visualSharp", {"position": v(-29, 23.78) * mm});
            skArc(sketch, "E270.filletArc", {"start": v(-31.37, 20.54) * mm, "mid": v(-30.58, 23.79) * mm, "end": v(-32.01, 26.8) * mm});
            skPoint(sketch, "E271.visualSharp", {"position": v(29, 23.78) * mm});
            skArc(sketch, "E271.filletArc", {"start": v(32.01, 26.8) * mm, "mid": v(30.58, 23.79) * mm, "end": v(31.37, 20.54) * mm});
            skPoint(sketch, "E272.visualSharp", {"position": v(80.08, 85) * mm});
            skArc(sketch, "E272.filletArc", {"start": v(78, 85) * mm, "mid": v(79.92, 85.38) * mm, "end": v(81.55, 86.47) * mm});
            skPoint(sketch, "E273.visualSharp", {"position": v(85, 80.02) * mm});
            skArc(sketch, "E273.filletArc", {"start": v(86.46, 81.48) * mm, "mid": v(85.38, 79.86) * mm, "end": v(85, 77.95) * mm});
            skPoint(sketch, "E274.visualSharp", {"position": v(-80.08, 85) * mm});
            skArc(sketch, "E274.filletArc", {"start": v(-81.55, 86.47) * mm, "mid": v(-79.92, 85.38) * mm, "end": v(-78, 85) * mm});
            skPoint(sketch, "E275.visualSharp", {"position": v(-85, 80.02) * mm});
            skArc(sketch, "E275.filletArc", {"start": v(-85, 77.95) * mm, "mid": v(-85.38, 79.86) * mm, "end": v(-86.46, 81.48) * mm});
            skArc(sketch, "E276.trimOffspring", {"start": v(31.37, -20.54) * mm, "mid": v(37.5, 0) * mm, "end": v(31.37, 20.54) * mm});
            skLineSegment(sketch, "E277.trimOffspring", {"start": v(-20.84, -75) * mm, "end": v(-51.3, -75) * mm});
            skPoint(sketch, "E278.visualSharp", {"position": v(-29, -23.78) * mm});
            skArc(sketch, "E278.filletArc", {"start": v(-32.01, -26.8) * mm, "mid": v(-30.58, -23.79) * mm, "end": v(-31.37, -20.54) * mm});
            skPoint(sketch, "E279.visualSharp", {"position": v(24.07, -28.75) * mm});
            skPoint(sketch, "E280.visualSharp", {"position": v(29, -23.78) * mm});
            skArc(sketch, "E280.filletArc", {"start": v(31.37, -20.54) * mm, "mid": v(30.58, -23.79) * mm, "end": v(32.01, -26.8) * mm});
            skPoint(sketch, "E281.visualSharp", {"position": v(75, -69.98) * mm});
            skArc(sketch, "E281.filletArc", {"start": v(66.46, -61.4) * mm, "mid": v(71.9, -62.5) * mm, "end": v(75, -57.87) * mm});
            skPoint(sketch, "E282.visualSharp", {"position": v(70.12, -75) * mm});
            skArc(sketch, "E282.filletArc", {"start": v(58.09, -75) * mm, "mid": v(62.7, -71.92) * mm, "end": v(61.63, -66.47) * mm});
            skPoint(sketch, "E283.visualSharp", {"position": v(-75, -69.98) * mm});
            skArc(sketch, "E283.filletArc", {"start": v(-75, -57.87) * mm, "mid": v(-71.9, -62.5) * mm, "end": v(-66.46, -61.4) * mm});
            skPoint(sketch, "E284.visualSharp", {"position": v(-70.12, -75) * mm});
            skArc(sketch, "E284.filletArc", {"start": v(-61.63, -66.47) * mm, "mid": v(-62.7, -71.92) * mm, "end": v(-58.09, -75) * mm});
            skArc(sketch, "E285.filletArc", {"start": v(-28.1, -40.88) * mm, "mid": v(-31.74, -38.9) * mm, "end": v(-35.63, -40.36) * mm});
            skArc(sketch, "E286.filletArc", {"start": v(35.63, -40.36) * mm, "mid": v(31.74, -38.9) * mm, "end": v(28.1, -40.88) * mm});
            skPoint(sketch, "E287.visualSharp", {"position": v(15.2, -75) * mm});
            skArc(sketch, "E287.filletArc", {"start": v(15.9, -69.17) * mm, "mid": v(17.02, -73.23) * mm, "end": v(20.84, -75) * mm});
            skPoint(sketch, "E288.visualSharp", {"position": v(-15.2, -75) * mm});
            skArc(sketch, "E288.filletArc", {"start": v(-20.84, -75) * mm, "mid": v(-17.02, -73.23) * mm, "end": v(-15.9, -69.17) * mm});
            skPoint(sketch, "E289.visualSharp", {"position": v(85, -80.02) * mm});
            skArc(sketch, "E289.filletArc", {"start": v(85, -77.95) * mm, "mid": v(85.38, -79.86) * mm, "end": v(86.46, -81.48) * mm});
            skPoint(sketch, "E290.visualSharp", {"position": v(80.08, -85) * mm});
            skArc(sketch, "E290.filletArc", {"start": v(81.55, -86.47) * mm, "mid": v(79.92, -85.38) * mm, "end": v(78, -85) * mm});
            skPoint(sketch, "E291.visualSharp", {"position": v(-80.08, -85) * mm});
            skArc(sketch, "E291.filletArc", {"start": v(-78, -85) * mm, "mid": v(-79.92, -85.38) * mm, "end": v(-81.55, -86.47) * mm});
            skPoint(sketch, "E292.visualSharp", {"position": v(-85, -80.02) * mm});
            skArc(sketch, "E292.filletArc", {"start": v(-86.46, -81.48) * mm, "mid": v(-85.38, -79.86) * mm, "end": v(-85, -77.95) * mm});
            skSolve(sketch);
        }
        {
            var Q0;
            Q0=makeQuery(id+"F0.imprint","IMPRINT",FACE,{"disambiguationData":[TD([[makeQuery(id+"F0.imprint","IMPRINT",EDGE,{"derivedFrom":sQuery(id+"F0.wireOp",EDGE,"c74cb722-dff2-409a-bd8e-8c5674c5de5c")}),1.0]])]});
            var Q1;
            Q1=makeQuery(id+"F0.imprint","IMPRINT",FACE,{"disambiguationData":[TD([[makeQuery(id+"F0.imprint","IMPRINT",EDGE,{"derivedFrom":sQuery(id+"F0.wireOp",EDGE,"E7.rect.bottom")}),-1.0]])]});
            var Q2;
            Q2=makeQuery(id+"F0.imprint","IMPRINT",FACE,{"disambiguationData":[TD([[makeQuery(id+"F0.imprint","IMPRINT",EDGE,{"derivedFrom":sQuery(id+"F0.wireOp",EDGE,"E7.rect.bottom")}),1.0]])]});
            extrude(context, id + "F1", {"entities" : qUnion([Q0, Q1, Q2]), "depth" : 2 * mm});
        }
        {
            var Q0;
            Q0=makeQuery(id+"F1.opExtrude","CAP_FACE",FACE,{"disambiguationData":[OSD([sQuery(id+"F0.wireOp",EDGE,"E8.0"),sQuery(id+"F0.wireOp",EDGE,"E8.1"),sQuery(id+"F0.wireOp",EDGE,"E8.2"),sQuery(id+"F0.wireOp",EDGE,"E8.3"),sQuery(id+"F0.wireOp",EDGE,"E9.0"),sQuery(id+"F0.wireOp",EDGE,"E9.1"),sQuery(id+"F0.wireOp",EDGE,"E9.2"),sQuery(id+"F0.wireOp",EDGE,"E9.3"),sQuery(id+"F0.wireOp",EDGE,"E12.trimOffspring"),sQuery(id+"F0.wireOp",EDGE,"E13.trimOffspring"),sQuery(id+"F0.wireOp",EDGE,"E14.trimOffspring"),sQuery(id+"F0.wireOp",EDGE,"E15.trimOffspring"),sQuery(id+"F0.wireOp",EDGE,"E20.0"),sQuery(id+"F0.wireOp",EDGE,"E21.0"),sQuery(id+"F0.wireOp",EDGE,"E22.0"),sQuery(id+"F0.wireOp",EDGE,"E23.0"),sQuery(id+"F0.wireOp",EDGE,"E24.0"),sQuery(id+"F0.wireOp",EDGE,"E25.0"),sQuery(id+"F0.wireOp",EDGE,"E26.0"),sQuery(id+"F0.wireOp",EDGE,"E27.0"),sQuery(id+"F0.wireOp",EDGE,"E48.filletArc"),sQuery(id+"F0.wireOp",EDGE,"E49.filletArc"),sQuery(id+"F0.wireOp",EDGE,"E53.filletArc"),sQuery(id+"F0.wireOp",EDGE,"E54.filletArc"),sQuery(id+"F0.wireOp",EDGE,"E59.filletArc"),sQuery(id+"F0.wireOp",EDGE,"E60.filletArc"),sQuery(id+"F0.wireOp",EDGE,"E66.filletArc"),sQuery(id+"F0.wireOp",EDGE,"E67.filletArc"),sQuery(id+"F0.wireOp",EDGE,"E79"),sQuery(id+"F0.wireOp",EDGE,"E80"),sQuery(id+"F0.wireOp",EDGE,"E81"),sQuery(id+"F0.wireOp",EDGE,"E82"),sQuery(id+"F0.wireOp",EDGE,"E83"),sQuery(id+"F0.wireOp",EDGE,"E87.MirrorC"),sQuery(id+"F0.wireOp",EDGE,"E84"),sQuery(id+"F0.wireOp",EDGE,"E88.MirrorC"),sQuery(id+"F0.wireOp",EDGE,"E89.filletArc"),sQuery(id+"F0.wireOp",EDGE,"E90.filletArc"),sQuery(id+"F0.wireOp",EDGE,"E91.filletArc"),sQuery(id+"F0.wireOp",EDGE,"E92.filletArc"),sQuery(id+"F0.wireOp",EDGE,"E93.filletArc"),sQuery(id+"F0.wireOp",EDGE,"E94.filletArc"),sQuery(id+"F0.wireOp",EDGE,"E95.filletArc"),sQuery(id+"F0.wireOp",EDGE,"E96.filletArc"),sQuery(id+"F0.wireOp",EDGE,"E97.filletArc"),sQuery(id+"F0.wireOp",EDGE,"E98.filletArc"),sQuery(id+"F0.wireOp",EDGE,"E99.filletArc"),sQuery(id+"F0.wireOp",EDGE,"E100.filletArc"),sQuery(id+"F0.wireOp",EDGE,"E101"),sQuery(id+"F0.wireOp",EDGE,"E102"),sQuery(id+"F0.wireOp",EDGE,"E103"),sQuery(id+"F0.wireOp",EDGE,"E108"),sQuery(id+"F0.wireOp",EDGE,"E109"),sQuery(id+"F0.wireOp",EDGE,"E110.trimOffspring"),sQuery(id+"F0.wireOp",EDGE,"E111.trimOffspring"),sQuery(id+"F0.wireOp",EDGE,"E112.trimOffspring"),sQuery(id+"F0.wireOp",EDGE,"E113.filletArc"),sQuery(id+"F0.wireOp",EDGE,"E114.filletArc"),sQuery(id+"F0.wireOp",EDGE,"E115.filletArc"),sQuery(id+"F0.wireOp",EDGE,"E116.filletArc"),sQuery(id+"F0.wireOp",EDGE,"E117.trimOffspring"),sQuery(id+"F0.wireOp",EDGE,"E118.trimOffspring"),sQuery(id+"F0.wireOp",EDGE,"E119.trimOffspring"),sQuery(id+"F0.wireOp",EDGE,"E120.filletArc"),sQuery(id+"F0.wireOp",EDGE,"E121.filletArc"),sQuery(id+"F0.wireOp",EDGE,"E122.filletArc"),sQuery(id+"F0.wireOp",EDGE,"E123.filletArc"),sQuery(id+"F0.wireOp",EDGE,"E124"),sQuery(id+"F0.wireOp",EDGE,"E125"),sQuery(id+"F0.wireOp",EDGE,"E126"),sQuery(id+"F0.wireOp",EDGE,"E127"),sQuery(id+"F0.wireOp",EDGE,"E128"),sQuery(id+"F0.wireOp",EDGE,"E129"),sQuery(id+"F0.wireOp",EDGE,"E130"),sQuery(id+"F0.wireOp",EDGE,"E131"),sQuery(id+"F0.wireOp",EDGE,"E132"),sQuery(id+"F0.wireOp",EDGE,"E133"),sQuery(id+"F0.wireOp",EDGE,"E134"),sQuery(id+"F0.wireOp",EDGE,"E135.MirrorCS"),sQuery(id+"F0.wireOp",EDGE,"E136.MirrorCS"),sQuery(id+"F0.wireOp",EDGE,"E137.MirrorC"),sQuery(id+"F0.wireOp",EDGE,"E138.MirrorCS"),sQuery(id+"F0.wireOp",EDGE,"E139.MirrorCS"),sQuery(id+"F0.wireOp",EDGE,"E140.MirrorCS"),sQuery(id+"F0.wireOp",EDGE,"E141.MirrorCS"),sQuery(id+"F0.wireOp",EDGE,"E142.MirrorC"),sQuery(id+"F0.wireOp",EDGE,"E143.MirrorCS"),sQuery(id+"F0.wireOp",EDGE,"E144.MirrorCS"),sQuery(id+"F0.wireOp",EDGE,"E145.MirrorCS"),sQuery(id+"F0.wireOp",EDGE,"E146.MirrorCS"),sQuery(id+"F0.wireOp",EDGE,"E147.MirrorCS"),sQuery(id+"F0.wireOp",EDGE,"E148.MirrorCS"),sQuery(id+"F0.wireOp",EDGE,"E150"),sQuery(id+"F0.wireOp",EDGE,"E151"),sQuery(id+"F0.wireOp",EDGE,"E152.trimOffspring"),sQuery(id+"F0.wireOp",EDGE,"E153.filletArc"),sQuery(id+"F0.wireOp",EDGE,"E154.filletArc"),sQuery(id+"F0.wireOp",EDGE,"E155.MirrorC"),sQuery(id+"F0.wireOp",EDGE,"E156.MirrorCS"),sQuery(id+"F0.wireOp",EDGE,"E157.MirrorCS"),sQuery(id+"F0.wireOp",EDGE,"E158.MirrorCS"),sQuery(id+"F0.wireOp",EDGE,"E159.trimOffspring"),sQuery(id+"F0.wireOp",EDGE,"E160.trimOffspring"),sQuery(id+"F0.wireOp",EDGE,"E161.trimOffspring"),sQuery(id+"F0.wireOp",EDGE,"E162.trimOffspring"),sQuery(id+"F0.wireOp",EDGE,"E163.trimOffspring"),sQuery(id+"F0.wireOp",EDGE,"E164.MirrorCS"),sQuery(id+"F0.wireOp",EDGE,"E165.MirrorCS"),sQuery(id+"F0.wireOp",EDGE,"E166.MirrorCS"),sQuery(id+"F0.wireOp",EDGE,"E167.MirrorCS"),sQuery(id+"F0.wireOp",EDGE,"E168.MirrorCS"),sQuery(id+"F0.wireOp",EDGE,"E169.MirrorCS"),sQuery(id+"F0.wireOp",EDGE,"E170.MirrorCS"),sQuery(id+"F0.wireOp",EDGE,"E171.MirrorCS"),sQuery(id+"F0.wireOp",EDGE,"E172.MirrorCS"),sQuery(id+"F0.wireOp",EDGE,"E173.MirrorCS"),sQuery(id+"F0.wireOp",EDGE,"E174.MirrorCS"),sQuery(id+"F0.wireOp",EDGE,"E175.MirrorCS"),sQuery(id+"F0.wireOp",EDGE,"E176.MirrorCS"),sQuery(id+"F0.wireOp",EDGE,"E177.MirrorCS"),sQuery(id+"F0.wireOp",EDGE,"E178.MirrorCS"),sQuery(id+"F0.wireOp",EDGE,"E179.MirrorCS"),sQuery(id+"F0.wireOp",EDGE,"E180.MirrorCS"),sQuery(id+"F0.wireOp",EDGE,"E181.MirrorCS"),sQuery(id+"F0.wireOp",EDGE,"E182.MirrorCS"),sQuery(id+"F0.wireOp",EDGE,"E183.MirrorCS"),sQuery(id+"F0.wireOp",EDGE,"E184.MirrorC"),sQuery(id+"F0.wireOp",EDGE,"E185.MirrorC"),sQuery(id+"F0.wireOp",EDGE,"E186.MirrorC"),sQuery(id+"F0.wireOp",EDGE,"E187.MirrorC"),sQuery(id+"F0.wireOp",EDGE,"E188.MirrorC"),sQuery(id+"F0.wireOp",EDGE,"E189.MirrorCS"),sQuery(id+"F0.wireOp",EDGE,"E190.MirrorCS"),sQuery(id+"F0.wireOp",EDGE,"E191.MirrorCS"),sQuery(id+"F0.wireOp",EDGE,"E192.MirrorCS"),sQuery(id+"F0.wireOp",EDGE,"E193.MirrorCS"),sQuery(id+"F0.wireOp",EDGE,"E194.MirrorCS"),sQuery(id+"F0.wireOp",EDGE,"E195.MirrorC"),sQuery(id+"F0.wireOp",EDGE,"E196.MirrorCS"),sQuery(id+"F0.wireOp",EDGE,"E197.MirrorCS"),sQuery(id+"F0.wireOp",EDGE,"E198.MirrorCS"),sQuery(id+"F0.wireOp",EDGE,"E199.trimOffspring"),sQuery(id+"F0.wireOp",EDGE,"E200.trimOffspring"),sQuery(id+"F0.wireOp",EDGE,"E201.trimOffspring"),sQuery(id+"F0.wireOp",EDGE,"E202.trimOffspring"),sQuery(id+"F0.wireOp",EDGE,"E203.trimOffspring"),sQuery(id+"F0.wireOp",EDGE,"E204.trimOffspring"),sQuery(id+"F0.wireOp",EDGE,"E205.MirrorCS"),sQuery(id+"F0.wireOp",EDGE,"E206.trimOffspring"),sQuery(id+"F0.wireOp",EDGE,"E207.trimOffspring"),sQuery(id+"F0.wireOp",EDGE,"E208.trimOffspring"),sQuery(id+"F0.wireOp",EDGE,"E209.trimOffspring"),sQuery(id+"F0.wireOp",EDGE,"E213"),sQuery(id+"F0.wireOp",EDGE,"E215"),sQuery(id+"F0.wireOp",EDGE,"E216.MirrorC"),sQuery(id+"F0.wireOp",EDGE,"E217.MirrorC"),sQuery(id+"F0.wireOp",EDGE,"E219"),sQuery(id+"F0.wireOp",EDGE,"E220"),sQuery(id+"F0.wireOp",EDGE,"E221"),sQuery(id+"F0.wireOp",EDGE,"E222"),sQuery(id+"F0.wireOp",EDGE,"E223"),sQuery(id+"F0.wireOp",EDGE,"E224"),sQuery(id+"F0.wireOp",EDGE,"E225"),sQuery(id+"F0.wireOp",EDGE,"E226"),sQuery(id+"F0.wireOp",EDGE,"E227"),sQuery(id+"F0.wireOp",EDGE,"E228"),sQuery(id+"F0.wireOp",EDGE,"E229"),sQuery(id+"F0.wireOp",EDGE,"E230"),sQuery(id+"F0.wireOp",EDGE,"E231"),sQuery(id+"F0.wireOp",EDGE,"E234"),sQuery(id+"F0.wireOp",EDGE,"E235"),sQuery(id+"F0.wireOp",EDGE,"E236"),sQuery(id+"F0.wireOp",EDGE,"E237"),sQuery(id+"F0.wireOp",EDGE,"E238"),sQuery(id+"F0.wireOp",EDGE,"E239"),sQuery(id+"F0.wireOp",EDGE,"E240"),sQuery(id+"F0.wireOp",EDGE,"E241"),sQuery(id+"F0.wireOp",EDGE,"E243"),sQuery(id+"F0.wireOp",EDGE,"E244"),sQuery(id+"F0.wireOp",EDGE,"E245"),sQuery(id+"F0.wireOp",EDGE,"E246"),sQuery(id+"F0.wireOp",EDGE,"E247"),sQuery(id+"F0.wireOp",EDGE,"E248"),sQuery(id+"F0.wireOp",EDGE,"E250"),sQuery(id+"F0.wireOp",EDGE,"E251"),sQuery(id+"F0.wireOp",EDGE,"E252.trimOffspring"),sQuery(id+"F0.wireOp",EDGE,"E253.trimOffspring"),sQuery(id+"F0.wireOp",EDGE,"E254.trimOffspring"),sQuery(id+"F0.wireOp",EDGE,"E255.trimOffspring"),sQuery(id+"F0.wireOp",EDGE,"E256.trimOffspring"),sQuery(id+"F0.wireOp",EDGE,"E257.trimOffspring"),sQuery(id+"F0.wireOp",EDGE,"E258.trimOffspring"),sQuery(id+"F0.wireOp",EDGE,"E259.trimOffspring"),sQuery(id+"F0.wireOp",EDGE,"E260.filletArc"),sQuery(id+"F0.wireOp",EDGE,"E261.filletArc"),sQuery(id+"F0.wireOp",EDGE,"E262.filletArc"),sQuery(id+"F0.wireOp",EDGE,"E263.filletArc"),sQuery(id+"F0.wireOp",EDGE,"E264.filletArc"),sQuery(id+"F0.wireOp",EDGE,"E265.filletArc"),sQuery(id+"F0.wireOp",EDGE,"E266.trimOffspring"),sQuery(id+"F0.wireOp",EDGE,"E267.filletArc"),sQuery(id+"F0.wireOp",EDGE,"E268.filletArc"),sQuery(id+"F0.wireOp",EDGE,"E270.filletArc"),sQuery(id+"F0.wireOp",EDGE,"E271.filletArc"),sQuery(id+"F0.wireOp",EDGE,"E272.filletArc"),sQuery(id+"F0.wireOp",EDGE,"E273.filletArc"),sQuery(id+"F0.wireOp",EDGE,"E274.filletArc"),sQuery(id+"F0.wireOp",EDGE,"E275.filletArc"),sQuery(id+"F0.wireOp",EDGE,"E276.trimOffspring"),sQuery(id+"F0.wireOp",EDGE,"E277.trimOffspring"),sQuery(id+"F0.wireOp",EDGE,"E278.filletArc"),sQuery(id+"F0.wireOp",EDGE,"E280.filletArc"),sQuery(id+"F0.wireOp",EDGE,"E281.filletArc"),sQuery(id+"F0.wireOp",EDGE,"E282.filletArc"),sQuery(id+"F0.wireOp",EDGE,"E283.filletArc"),sQuery(id+"F0.wireOp",EDGE,"E284.filletArc"),sQuery(id+"F0.wireOp",EDGE,"E285.filletArc"),sQuery(id+"F0.wireOp",EDGE,"E286.filletArc"),sQuery(id+"F0.wireOp",EDGE,"E287.filletArc"),sQuery(id+"F0.wireOp",EDGE,"E288.filletArc"),sQuery(id+"F0.wireOp",EDGE,"E289.filletArc"),sQuery(id+"F0.wireOp",EDGE,"E290.filletArc"),sQuery(id+"F0.wireOp",EDGE,"E291.filletArc"),sQuery(id+"F0.wireOp",EDGE,"E292.filletArc")])],"isStart":false});
            var sketch = newSketch(context, id + "F2", { "sketchPlane" : qUnion([Q0])});
            skArc(sketch, "E293", {"start": v(-26.9, 42.5) * mm, "mid": v(-19.91, 55.22) * mm, "end": v(-15.9, 69.17) * mm});
            skArc(sketch, "E294", {"start": v(26.93, 42.47) * mm, "mid": v(19.92, 55.2) * mm, "end": v(15.9, 69.17) * mm});
            skArc(sketch, "E295", {"start": v(26.88, -42.54) * mm, "mid": v(18.04, -60.35) * mm, "end": v(15, -80) * mm});
            skArc(sketch, "E296", {"start": v(-26.9, -42.51) * mm, "mid": v(-18.05, -60.34) * mm, "end": v(-15, -80) * mm});
            skArc(sketch, "E297", {"start": v(-31.93, 19.6) * mm, "mid": v(-37.47, -0.06) * mm, "end": v(-31.87, -19.7) * mm});
            skArc(sketch, "E298", {"start": v(-32.46, 18.78) * mm, "mid": v(-28.3, 28.46) * mm, "end": v(-27.78, 38.98) * mm});
            skArc(sketch, "E299", {"start": v(27.82, 39) * mm, "mid": v(28.43, 28.34) * mm, "end": v(32.61, 18.51) * mm});
            skArc(sketch, "E300", {"start": v(32.3, -19.07) * mm, "mid": v(28.17, -28.58) * mm, "end": v(27.74, -38.94) * mm});
            skArc(sketch, "E301", {"start": v(-27.77, -38.96) * mm, "mid": v(-28.15, -28.98) * mm, "end": v(-31.87, -19.7) * mm});
            skLineSegment(sketch, "E302", {"start": v(-10, 85) * mm, "end": v(10, 85) * mm});
            skLineSegment(sketch, "E303", {"start": v(-10, -85) * mm, "end": v(10, -85) * mm});
            skArc(sketch, "E304.trimOffspring", {"start": v(31.77, -19.87) * mm, "mid": v(37.47, -0.3) * mm, "end": v(32.09, 19.35) * mm});
            skPoint(sketch, "E305.visualSharp", {"position": v(-15.2, 85) * mm});
            skPoint(sketch, "E306.visualSharp", {"position": v(15.2, 85) * mm});
            skPoint(sketch, "E307.visualSharp", {"position": v(28.1, 40.88) * mm});
            skArc(sketch, "E307.filletArc", {"start": v(27.82, 39) * mm, "mid": v(27.7, 40.82) * mm, "end": v(26.93, 42.47) * mm});
            skPoint(sketch, "E308.visualSharp", {"position": v(-28.1, 40.88) * mm});
            skArc(sketch, "E308.filletArc", {"start": v(-26.9, 42.5) * mm, "mid": v(-27.68, 40.82) * mm, "end": v(-27.78, 38.98) * mm});
            skPoint(sketch, "E309.visualSharp", {"position": v(-28.1, -40.88) * mm});
            skArc(sketch, "E309.filletArc", {"start": v(-27.77, -38.96) * mm, "mid": v(-27.67, -40.82) * mm, "end": v(-26.9, -42.51) * mm});
            skPoint(sketch, "E310.visualSharp", {"position": v(28.1, -40.88) * mm});
            skArc(sketch, "E310.filletArc", {"start": v(26.88, -42.54) * mm, "mid": v(27.66, -40.82) * mm, "end": v(27.74, -38.94) * mm});
            skPoint(sketch, "E311.visualSharp", {"position": v(15.2, -85) * mm});
            skArc(sketch, "E311.filletArc", {"start": v(10, -85) * mm, "mid": v(13.54, -83.54) * mm, "end": v(15, -80) * mm});
            skPoint(sketch, "E312.visualSharp", {"position": v(-15.2, -85) * mm});
            skArc(sketch, "E312.filletArc", {"start": v(-15, -80) * mm, "mid": v(-13.54, -83.54) * mm, "end": v(-10, -85) * mm});
            skCircle(sketch, "E313", {"center": v(-24.76, 40.1) * mm, "radius": 1.5 * mm});
            skCircle(sketch, "E314.MirrorC", {"center": v(-11.33, -81.5) * mm, "radius": 1.5 * mm});
            skCircle(sketch, "E315.MirrorC", {"center": v(-24.76, -40.1) * mm, "radius": 1.5 * mm});
            skCircle(sketch, "E316.MirrorC", {"center": v(24.76, 40.1) * mm, "radius": 1.5 * mm});
            skCircle(sketch, "E317.MirrorC", {"center": v(24.76, -40.1) * mm, "radius": 1.5 * mm});
            skCircle(sketch, "E318.MirrorC", {"center": v(11.33, -81.5) * mm, "radius": 1.5 * mm});
            skArc(sketch, "E319", {"start": v(-15.9, 69.17) * mm, "mid": v(-17.02, 73.23) * mm, "end": v(-20.84, 75) * mm});
            skArc(sketch, "E320", {"start": v(15.9, 69.17) * mm, "mid": v(17.02, 73.23) * mm, "end": v(20.84, 75) * mm});
            skLineSegment(sketch, "E321", {"start": v(-20.84, 85) * mm, "end": v(20.84, 85) * mm});
            skArc(sketch, "E322", {"start": v(-20.84, 85) * mm, "mid": v(-25.84, 80) * mm, "end": v(-20.84, 75) * mm});
            skArc(sketch, "E323", {"start": v(20.84, 85) * mm, "mid": v(25.84, 80) * mm, "end": v(20.84, 75) * mm});
            skCircle(sketch, "E324", {"center": v(-22.84, 80) * mm, "radius": 1.5 * mm});
            skCircle(sketch, "E325.MirrorC", {"center": v(22.84, 80) * mm, "radius": 1.5 * mm});
            skPoint(sketch, "E326.orphan", {"position": v(0, 75) * mm});
            skPoint(sketch, "E327.end.orphan", {"position": v(0, -75) * mm});
            skArc(sketch, "E328.0", {"start": v(-47.34, -148.07) * mm, "mid": v(-24.35, -131.02) * mm, "end": v(-9.36, -106.64) * mm});
            skArc(sketch, "E328.1", {"start": v(-51.26, -151.44) * mm, "mid": v(-49.52, -149.5) * mm, "end": v(-47.34, -148.07) * mm});
            skArc(sketch, "E328.2", {"start": v(-56.43, -151.73) * mm, "mid": v(-53.86, -151.24) * mm, "end": v(-51.26, -151.44) * mm});
            skArc(sketch, "E328.3", {"start": v(-129.7, -136.84) * mm, "mid": v(-95.03, -153.99) * mm, "end": v(-56.43, -151.73) * mm});
            skArc(sketch, "E328.4", {"start": v(-134.33, -134.56) * mm, "mid": v(-131.86, -135.4) * mm, "end": v(-129.7, -136.84) * mm});
            skArc(sketch, "E328.5", {"start": v(-136.63, -129.93) * mm, "mid": v(-135.18, -132.1) * mm, "end": v(-134.33, -134.56) * mm});
            skArc(sketch, "E328.6", {"start": v(-151.76, -56.55) * mm, "mid": v(-153.94, -95.25) * mm, "end": v(-136.63, -129.93) * mm});
            skArc(sketch, "E328.7", {"start": v(-151.48, -51.38) * mm, "mid": v(-151.28, -53.98) * mm, "end": v(-151.76, -56.55) * mm});
            skArc(sketch, "E328.8", {"start": v(-148.12, -47.45) * mm, "mid": v(-149.54, -49.64) * mm, "end": v(-151.48, -51.38) * mm});
            skArc(sketch, "E328.9", {"start": v(-106.64, -9.36) * mm, "mid": v(-131.07, -24.4) * mm, "end": v(-148.12, -47.45) * mm});
            skArc(sketch, "E328.10", {"start": v(-106.64, 9.36) * mm, "mid": v(-100.17, 0) * mm, "end": v(-106.64, -9.36) * mm});
            skArc(sketch, "E328.11", {"start": v(-9.36, -106.64) * mm, "mid": v(0, -100.17) * mm, "end": v(9.36, -106.64) * mm});
            skArc(sketch, "E328.12", {"start": v(-148.12, 47.45) * mm, "mid": v(-131.07, 24.4) * mm, "end": v(-106.64, 9.36) * mm});
            skArc(sketch, "E328.13", {"start": v(-151.48, 51.38) * mm, "mid": v(-149.54, 49.64) * mm, "end": v(-148.12, 47.45) * mm});
            skArc(sketch, "E328.14", {"start": v(-151.76, 56.55) * mm, "mid": v(-151.28, 53.98) * mm, "end": v(-151.48, 51.38) * mm});
            skArc(sketch, "E328.15", {"start": v(-136.63, 129.93) * mm, "mid": v(-153.94, 95.25) * mm, "end": v(-151.76, 56.55) * mm});
            skArc(sketch, "E328.16", {"start": v(-134.33, 134.56) * mm, "mid": v(-135.18, 132.1) * mm, "end": v(-136.63, 129.93) * mm});
            skArc(sketch, "E328.17", {"start": v(-129.7, 136.84) * mm, "mid": v(-131.86, 135.4) * mm, "end": v(-134.33, 134.56) * mm});
            skArc(sketch, "E328.18", {"start": v(-56.43, 151.73) * mm, "mid": v(-95.03, 153.99) * mm, "end": v(-129.7, 136.84) * mm});
            skArc(sketch, "E328.19", {"start": v(-51.26, 151.44) * mm, "mid": v(-53.86, 151.24) * mm, "end": v(-56.43, 151.73) * mm});
            skArc(sketch, "E328.20", {"start": v(-47.34, 148.07) * mm, "mid": v(-49.52, 149.5) * mm, "end": v(-51.26, 151.44) * mm});
            skArc(sketch, "E328.21", {"start": v(-9.36, 106.64) * mm, "mid": v(-24.35, 131.02) * mm, "end": v(-47.34, 148.07) * mm});
            skArc(sketch, "E328.22", {"start": v(148.12, -47.45) * mm, "mid": v(131.07, -24.4) * mm, "end": v(106.64, -9.36) * mm});
            skArc(sketch, "E328.23", {"start": v(151.48, -51.38) * mm, "mid": v(149.54, -49.64) * mm, "end": v(148.12, -47.45) * mm});
            skArc(sketch, "E328.24", {"start": v(151.76, -56.55) * mm, "mid": v(151.28, -53.98) * mm, "end": v(151.48, -51.38) * mm});
            skArc(sketch, "E328.25", {"start": v(136.63, -129.93) * mm, "mid": v(153.94, -95.25) * mm, "end": v(151.76, -56.55) * mm});
            skArc(sketch, "E328.26", {"start": v(134.33, -134.56) * mm, "mid": v(135.18, -132.1) * mm, "end": v(136.63, -129.93) * mm});
            skArc(sketch, "E328.27", {"start": v(129.7, -136.84) * mm, "mid": v(131.86, -135.4) * mm, "end": v(134.33, -134.56) * mm});
            skArc(sketch, "E328.28", {"start": v(9.36, -106.64) * mm, "mid": v(24.35, -131.02) * mm, "end": v(47.34, -148.07) * mm});
            skArc(sketch, "E328.29", {"start": v(47.34, -148.07) * mm, "mid": v(49.52, -149.5) * mm, "end": v(51.26, -151.44) * mm});
            skArc(sketch, "E328.30", {"start": v(51.26, -151.44) * mm, "mid": v(53.86, -151.24) * mm, "end": v(56.43, -151.73) * mm});
            skArc(sketch, "E328.31", {"start": v(56.43, -151.73) * mm, "mid": v(95.03, -153.99) * mm, "end": v(129.7, -136.84) * mm});
            skArc(sketch, "E328.32", {"start": v(106.64, -9.36) * mm, "mid": v(100.17, 0) * mm, "end": v(106.64, 9.36) * mm});
            skArc(sketch, "E328.33", {"start": v(106.64, 9.36) * mm, "mid": v(131.07, 24.4) * mm, "end": v(148.12, 47.45) * mm});
            skArc(sketch, "E328.34", {"start": v(148.12, 47.45) * mm, "mid": v(149.54, 49.64) * mm, "end": v(151.48, 51.38) * mm});
            skArc(sketch, "E328.35", {"start": v(151.48, 51.38) * mm, "mid": v(151.28, 53.98) * mm, "end": v(151.76, 56.55) * mm});
            skArc(sketch, "E328.36", {"start": v(151.76, 56.55) * mm, "mid": v(153.94, 95.25) * mm, "end": v(136.63, 129.93) * mm});
            skArc(sketch, "E328.37", {"start": v(136.63, 129.93) * mm, "mid": v(135.18, 132.1) * mm, "end": v(134.33, 134.56) * mm});
            skArc(sketch, "E328.38", {"start": v(134.33, 134.56) * mm, "mid": v(131.86, 135.4) * mm, "end": v(129.7, 136.84) * mm});
            skArc(sketch, "E328.39", {"start": v(129.7, 136.84) * mm, "mid": v(95.03, 153.99) * mm, "end": v(56.43, 151.73) * mm});
            skArc(sketch, "E328.40", {"start": v(56.43, 151.73) * mm, "mid": v(53.86, 151.24) * mm, "end": v(51.26, 151.44) * mm});
            skArc(sketch, "E328.41", {"start": v(51.26, 151.44) * mm, "mid": v(49.52, 149.5) * mm, "end": v(47.34, 148.07) * mm});
            skArc(sketch, "E328.42", {"start": v(47.34, 148.07) * mm, "mid": v(24.35, 131.02) * mm, "end": v(9.36, 106.64) * mm});
            skArc(sketch, "E328.43", {"start": v(9.36, 106.64) * mm, "mid": v(0, 100.17) * mm, "end": v(-9.36, 106.64) * mm});
            skCircle(sketch, "E329", {"center": v(-26.94, 60.87) * mm, "radius": 5 * mm});
            skArc(sketch, "E330", {"start": v(-26.9, 42.5) * mm, "mid": v(-25.92, 50.3) * mm, "end": v(-30.06, 56.97) * mm});
            skArc(sketch, "E331", {"start": v(-27.88, 65.78) * mm, "mid": v(-23.72, 70.73) * mm, "end": v(-24.9, 77.08) * mm});
            skCircle(sketch, "E332", {"center": v(-26.94, 60.87) * mm, "radius": 3.25 * mm});
            skSolve(sketch);
        }
        {
            var Q0;
            Q0=makeQuery(id+"F2.imprint","IMPRINT",FACE,{"disambiguationData":[TD([[makeQuery(id+"F2.imprint","IMPRINT",EDGE,{"derivedFrom":sQuery(id+"F2.wireOp",EDGE,"E293")}),1.0]])]});
            var Q1;
            Q1=makeQuery(id+"F2.imprint","IMPRINT",FACE,{"disambiguationData":[TD([[makeQuery(id+"F2.imprint","IMPRINT",EDGE,{"derivedFrom":makeQuery(id+"F1.opExtrude","CAP_EDGE",EDGE,{"disambiguationData":[OSD([sQuery(id+"F0.wireOp",EDGE,"E88.MirrorC")])],"isStart":false})}),-1.0]])]});
            var Q2;
            Q2=makeQuery(id+"F2.imprint","IMPRINT",FACE,{"disambiguationData":[TD([[makeQuery(id+"F2.imprint","IMPRINT",EDGE,{"derivedFrom":makeQuery(id+"F1.opExtrude","CAP_EDGE",EDGE,{"disambiguationData":[OSD([sQuery(id+"F0.wireOp",EDGE,"E81")])],"isStart":false})}),1.0]])]});
            var Q3;
            Q3=makeQuery(id+"F2.imprint","IMPRINT",FACE,{"disambiguationData":[TD([[makeQuery(id+"F2.imprint","IMPRINT",EDGE,{"derivedFrom":makeQuery(id+"F1.opExtrude","CAP_EDGE",EDGE,{"disambiguationData":[OSD([sQuery(id+"F0.wireOp",EDGE,"E82")])],"isStart":false})}),1.0]])]});
            var Q4;
            Q4=makeQuery(id+"F2.imprint","IMPRINT",FACE,{"disambiguationData":[TD([[makeQuery(id+"F2.imprint","IMPRINT",EDGE,{"derivedFrom":makeQuery(id+"F1.opExtrude","CAP_EDGE",EDGE,{"disambiguationData":[OSD([sQuery(id+"F0.wireOp",EDGE,"E87.MirrorC")])],"isStart":false})}),-1.0]])]});
            var Q5;
            Q5=makeQuery(id+"F2.imprint","IMPRINT",FACE,{"disambiguationData":[TD([[makeQuery(id+"F2.imprint","IMPRINT",EDGE,{"derivedFrom":makeQuery(id+"F1.opExtrude","CAP_EDGE",EDGE,{"disambiguationData":[OSD([sQuery(id+"F0.wireOp",EDGE,"E83")])],"isStart":false})}),1.0]])]});
            var Q6;
            Q6=makeQuery(id+"F2.imprint","IMPRINT",FACE,{"disambiguationData":[TD([[makeQuery(id+"F2.imprint","IMPRINT",EDGE,{"derivedFrom":makeQuery(id+"F1.opExtrude","CAP_EDGE",EDGE,{"disambiguationData":[OSD([sQuery(id+"F0.wireOp",EDGE,"E79")])],"isStart":false})}),1.0]])]});
            var Q7;
            Q7=makeQuery(id+"F2.imprint","IMPRINT",FACE,{"disambiguationData":[TD([[makeQuery(id+"F2.imprint","IMPRINT",EDGE,{"derivedFrom":makeQuery(id+"F1.opExtrude","CAP_EDGE",EDGE,{"disambiguationData":[OSD([sQuery(id+"F0.wireOp",EDGE,"E80")])],"isStart":false})}),1.0]])]});
            var Q8;
            Q8=makeQuery(id+"F2.imprint","IMPRINT",FACE,{"disambiguationData":[TD([[makeQuery(id+"F2.imprint","IMPRINT",EDGE,{"derivedFrom":makeQuery(id+"F1.opExtrude","CAP_EDGE",EDGE,{"disambiguationData":[OSD([sQuery(id+"F0.wireOp",EDGE,"E84")])],"isStart":false})}),-1.0]])]});
            var Q9;
            Q9=makeQuery(id+"F2.imprint","IMPRINT",FACE,{"disambiguationData":[TD([[makeQuery(id+"F2.imprint","IMPRINT",EDGE,{"derivedFrom":sQuery(id+"F2.wireOp",EDGE,"E293")}),-1.0]])]});
            var Q10;
            Q10=makeQuery(id+"F2.imprint","IMPRINT",FACE,{"disambiguationData":[TD([[makeQuery(id+"F2.imprint","IMPRINT",EDGE,{"derivedFrom":sQuery(id+"F2.wireOp",EDGE,"E332")}),-1.0]])]});
            var Q11;
            {var subQ0=sQuery(id+"F2.wireOp",EDGE,"E322");var subQ3=sQuery(id+"F2.wireOp",EDGE,"E331");var subQ4=makeQuery(id+"F2.imprint","INTERSECT",VERTEX,{"derivedFrom":[subQ0,subQ3]});Q11=makeQuery(id+"F2.imprint","IMPRINT",FACE,{"disambiguationData":[TD([[makeQuery(id+"F2.imprint","IMPRINT",EDGE,{"disambiguationData":[TD([[subQ4,1.0]])],"derivedFrom":subQ3}),-1.0]])]});}
            extrude(context, id + "F3", {"entities" : qUnion([Q0, Q1, Q2, Q3, Q4, Q5, Q6, Q7, Q8, Q9, Q10, Q11]), "depth" : 2 * mm});
        }
        {
            var Q0;
            Q0=sQuery(id+"F2.wireOp",VERTEX,"E324.center");
            var Q1;
            Q1=sQuery(id+"F2.wireOp",VERTEX,"E325.MirrorC.center");
            var Q2;
            Q2=sQuery(id+"F2.wireOp",VERTEX,"E316.MirrorC.center");
            var Q3;
            Q3=sQuery(id+"F2.wireOp",VERTEX,"E313.center");
            var Q4;
            Q4=sQuery(id+"F2.wireOp",VERTEX,"E317.MirrorC.center");
            var Q5;
            Q5=sQuery(id+"F2.wireOp",VERTEX,"E315.MirrorC.center");
            var Q6;
            Q6=sQuery(id+"F2.wireOp",VERTEX,"E318.MirrorC.center");
            var Q7;
            Q7=sQuery(id+"F2.wireOp",VERTEX,"E314.MirrorC.center");
            var Q8;
            Q8=makeQuery(id+"F1.opExtrude","SWEPT_BODY",BODY,{"disambiguationData":[OSD([sQuery(id+"F0.wireOp",EDGE,"E8.0"),sQuery(id+"F0.wireOp",EDGE,"E8.1"),sQuery(id+"F0.wireOp",EDGE,"E8.2"),sQuery(id+"F0.wireOp",EDGE,"E8.3"),sQuery(id+"F0.wireOp",EDGE,"E9.0"),sQuery(id+"F0.wireOp",EDGE,"E9.1"),sQuery(id+"F0.wireOp",EDGE,"E9.2"),sQuery(id+"F0.wireOp",EDGE,"E9.3"),sQuery(id+"F0.wireOp",EDGE,"E12.trimOffspring"),sQuery(id+"F0.wireOp",EDGE,"E13.trimOffspring"),sQuery(id+"F0.wireOp",EDGE,"E14.trimOffspring"),sQuery(id+"F0.wireOp",EDGE,"E15.trimOffspring"),sQuery(id+"F0.wireOp",EDGE,"E20.0"),sQuery(id+"F0.wireOp",EDGE,"E21.0"),sQuery(id+"F0.wireOp",EDGE,"E22.0"),sQuery(id+"F0.wireOp",EDGE,"E23.0"),sQuery(id+"F0.wireOp",EDGE,"E24.0"),sQuery(id+"F0.wireOp",EDGE,"E25.0"),sQuery(id+"F0.wireOp",EDGE,"E26.0"),sQuery(id+"F0.wireOp",EDGE,"E27.0"),sQuery(id+"F0.wireOp",EDGE,"E48.filletArc"),sQuery(id+"F0.wireOp",EDGE,"E49.filletArc"),sQuery(id+"F0.wireOp",EDGE,"E53.filletArc"),sQuery(id+"F0.wireOp",EDGE,"E54.filletArc"),sQuery(id+"F0.wireOp",EDGE,"E59.filletArc"),sQuery(id+"F0.wireOp",EDGE,"E60.filletArc"),sQuery(id+"F0.wireOp",EDGE,"E66.filletArc"),sQuery(id+"F0.wireOp",EDGE,"E67.filletArc"),sQuery(id+"F0.wireOp",EDGE,"E79"),sQuery(id+"F0.wireOp",EDGE,"E80"),sQuery(id+"F0.wireOp",EDGE,"E81"),sQuery(id+"F0.wireOp",EDGE,"E82"),sQuery(id+"F0.wireOp",EDGE,"E83"),sQuery(id+"F0.wireOp",EDGE,"E87.MirrorC"),sQuery(id+"F0.wireOp",EDGE,"E84"),sQuery(id+"F0.wireOp",EDGE,"E88.MirrorC"),sQuery(id+"F0.wireOp",EDGE,"E89.filletArc"),sQuery(id+"F0.wireOp",EDGE,"E90.filletArc"),sQuery(id+"F0.wireOp",EDGE,"E91.filletArc"),sQuery(id+"F0.wireOp",EDGE,"E92.filletArc"),sQuery(id+"F0.wireOp",EDGE,"E93.filletArc"),sQuery(id+"F0.wireOp",EDGE,"E94.filletArc"),sQuery(id+"F0.wireOp",EDGE,"E95.filletArc"),sQuery(id+"F0.wireOp",EDGE,"E96.filletArc"),sQuery(id+"F0.wireOp",EDGE,"E97.filletArc"),sQuery(id+"F0.wireOp",EDGE,"E98.filletArc"),sQuery(id+"F0.wireOp",EDGE,"E99.filletArc"),sQuery(id+"F0.wireOp",EDGE,"E100.filletArc"),sQuery(id+"F0.wireOp",EDGE,"E101"),sQuery(id+"F0.wireOp",EDGE,"E102"),sQuery(id+"F0.wireOp",EDGE,"E103"),sQuery(id+"F0.wireOp",EDGE,"E108"),sQuery(id+"F0.wireOp",EDGE,"E109"),sQuery(id+"F0.wireOp",EDGE,"E110.trimOffspring"),sQuery(id+"F0.wireOp",EDGE,"E111.trimOffspring"),sQuery(id+"F0.wireOp",EDGE,"E112.trimOffspring"),sQuery(id+"F0.wireOp",EDGE,"E113.filletArc"),sQuery(id+"F0.wireOp",EDGE,"E114.filletArc"),sQuery(id+"F0.wireOp",EDGE,"E115.filletArc"),sQuery(id+"F0.wireOp",EDGE,"E116.filletArc"),sQuery(id+"F0.wireOp",EDGE,"E117.trimOffspring"),sQuery(id+"F0.wireOp",EDGE,"E118.trimOffspring"),sQuery(id+"F0.wireOp",EDGE,"E119.trimOffspring"),sQuery(id+"F0.wireOp",EDGE,"E120.filletArc"),sQuery(id+"F0.wireOp",EDGE,"E121.filletArc"),sQuery(id+"F0.wireOp",EDGE,"E122.filletArc"),sQuery(id+"F0.wireOp",EDGE,"E123.filletArc"),sQuery(id+"F0.wireOp",EDGE,"E124"),sQuery(id+"F0.wireOp",EDGE,"E125"),sQuery(id+"F0.wireOp",EDGE,"E126"),sQuery(id+"F0.wireOp",EDGE,"E127"),sQuery(id+"F0.wireOp",EDGE,"E128"),sQuery(id+"F0.wireOp",EDGE,"E129"),sQuery(id+"F0.wireOp",EDGE,"E130"),sQuery(id+"F0.wireOp",EDGE,"E131"),sQuery(id+"F0.wireOp",EDGE,"E132"),sQuery(id+"F0.wireOp",EDGE,"E133"),sQuery(id+"F0.wireOp",EDGE,"E134"),sQuery(id+"F0.wireOp",EDGE,"E135.MirrorCS"),sQuery(id+"F0.wireOp",EDGE,"E136.MirrorCS"),sQuery(id+"F0.wireOp",EDGE,"E137.MirrorC"),sQuery(id+"F0.wireOp",EDGE,"E138.MirrorCS"),sQuery(id+"F0.wireOp",EDGE,"E139.MirrorCS"),sQuery(id+"F0.wireOp",EDGE,"E140.MirrorCS"),sQuery(id+"F0.wireOp",EDGE,"E141.MirrorCS"),sQuery(id+"F0.wireOp",EDGE,"E142.MirrorC"),sQuery(id+"F0.wireOp",EDGE,"E143.MirrorCS"),sQuery(id+"F0.wireOp",EDGE,"E144.MirrorCS"),sQuery(id+"F0.wireOp",EDGE,"E145.MirrorCS"),sQuery(id+"F0.wireOp",EDGE,"E146.MirrorCS"),sQuery(id+"F0.wireOp",EDGE,"E147.MirrorCS"),sQuery(id+"F0.wireOp",EDGE,"E148.MirrorCS"),sQuery(id+"F0.wireOp",EDGE,"E150"),sQuery(id+"F0.wireOp",EDGE,"E151"),sQuery(id+"F0.wireOp",EDGE,"E152.trimOffspring"),sQuery(id+"F0.wireOp",EDGE,"E153.filletArc"),sQuery(id+"F0.wireOp",EDGE,"E154.filletArc"),sQuery(id+"F0.wireOp",EDGE,"E155.MirrorC"),sQuery(id+"F0.wireOp",EDGE,"E156.MirrorCS"),sQuery(id+"F0.wireOp",EDGE,"E157.MirrorCS"),sQuery(id+"F0.wireOp",EDGE,"E158.MirrorCS"),sQuery(id+"F0.wireOp",EDGE,"E159.trimOffspring"),sQuery(id+"F0.wireOp",EDGE,"E160.trimOffspring"),sQuery(id+"F0.wireOp",EDGE,"E161.trimOffspring"),sQuery(id+"F0.wireOp",EDGE,"E162.trimOffspring"),sQuery(id+"F0.wireOp",EDGE,"E163.trimOffspring"),sQuery(id+"F0.wireOp",EDGE,"E164.MirrorCS"),sQuery(id+"F0.wireOp",EDGE,"E165.MirrorCS"),sQuery(id+"F0.wireOp",EDGE,"E166.MirrorCS"),sQuery(id+"F0.wireOp",EDGE,"E167.MirrorCS"),sQuery(id+"F0.wireOp",EDGE,"E168.MirrorCS"),sQuery(id+"F0.wireOp",EDGE,"E169.MirrorCS"),sQuery(id+"F0.wireOp",EDGE,"E170.MirrorCS"),sQuery(id+"F0.wireOp",EDGE,"E171.MirrorCS"),sQuery(id+"F0.wireOp",EDGE,"E172.MirrorCS"),sQuery(id+"F0.wireOp",EDGE,"E173.MirrorCS"),sQuery(id+"F0.wireOp",EDGE,"E174.MirrorCS"),sQuery(id+"F0.wireOp",EDGE,"E175.MirrorCS"),sQuery(id+"F0.wireOp",EDGE,"E176.MirrorCS"),sQuery(id+"F0.wireOp",EDGE,"E177.MirrorCS"),sQuery(id+"F0.wireOp",EDGE,"E178.MirrorCS"),sQuery(id+"F0.wireOp",EDGE,"E179.MirrorCS"),sQuery(id+"F0.wireOp",EDGE,"E180.MirrorCS"),sQuery(id+"F0.wireOp",EDGE,"E181.MirrorCS"),sQuery(id+"F0.wireOp",EDGE,"E182.MirrorCS"),sQuery(id+"F0.wireOp",EDGE,"E183.MirrorCS"),sQuery(id+"F0.wireOp",EDGE,"E184.MirrorC"),sQuery(id+"F0.wireOp",EDGE,"E185.MirrorC"),sQuery(id+"F0.wireOp",EDGE,"E186.MirrorC"),sQuery(id+"F0.wireOp",EDGE,"E187.MirrorC"),sQuery(id+"F0.wireOp",EDGE,"E188.MirrorC"),sQuery(id+"F0.wireOp",EDGE,"E189.MirrorCS"),sQuery(id+"F0.wireOp",EDGE,"E190.MirrorCS"),sQuery(id+"F0.wireOp",EDGE,"E191.MirrorCS"),sQuery(id+"F0.wireOp",EDGE,"E192.MirrorCS"),sQuery(id+"F0.wireOp",EDGE,"E193.MirrorCS"),sQuery(id+"F0.wireOp",EDGE,"E194.MirrorCS"),sQuery(id+"F0.wireOp",EDGE,"E195.MirrorC"),sQuery(id+"F0.wireOp",EDGE,"E196.MirrorCS"),sQuery(id+"F0.wireOp",EDGE,"E197.MirrorCS"),sQuery(id+"F0.wireOp",EDGE,"E198.MirrorCS"),sQuery(id+"F0.wireOp",EDGE,"E199.trimOffspring"),sQuery(id+"F0.wireOp",EDGE,"E200.trimOffspring"),sQuery(id+"F0.wireOp",EDGE,"E201.trimOffspring"),sQuery(id+"F0.wireOp",EDGE,"E202.trimOffspring"),sQuery(id+"F0.wireOp",EDGE,"E203.trimOffspring"),sQuery(id+"F0.wireOp",EDGE,"E204.trimOffspring"),sQuery(id+"F0.wireOp",EDGE,"E205.MirrorCS"),sQuery(id+"F0.wireOp",EDGE,"E206.trimOffspring"),sQuery(id+"F0.wireOp",EDGE,"E207.trimOffspring"),sQuery(id+"F0.wireOp",EDGE,"E208.trimOffspring"),sQuery(id+"F0.wireOp",EDGE,"E209.trimOffspring"),sQuery(id+"F0.wireOp",EDGE,"E213"),sQuery(id+"F0.wireOp",EDGE,"E215"),sQuery(id+"F0.wireOp",EDGE,"E216.MirrorC"),sQuery(id+"F0.wireOp",EDGE,"E217.MirrorC"),sQuery(id+"F0.wireOp",EDGE,"E219"),sQuery(id+"F0.wireOp",EDGE,"E220"),sQuery(id+"F0.wireOp",EDGE,"E221"),sQuery(id+"F0.wireOp",EDGE,"E222"),sQuery(id+"F0.wireOp",EDGE,"E223"),sQuery(id+"F0.wireOp",EDGE,"E224"),sQuery(id+"F0.wireOp",EDGE,"E225"),sQuery(id+"F0.wireOp",EDGE,"E226"),sQuery(id+"F0.wireOp",EDGE,"E227"),sQuery(id+"F0.wireOp",EDGE,"E228"),sQuery(id+"F0.wireOp",EDGE,"E229"),sQuery(id+"F0.wireOp",EDGE,"E230"),sQuery(id+"F0.wireOp",EDGE,"E231"),sQuery(id+"F0.wireOp",EDGE,"E234"),sQuery(id+"F0.wireOp",EDGE,"E235"),sQuery(id+"F0.wireOp",EDGE,"E236"),sQuery(id+"F0.wireOp",EDGE,"E237"),sQuery(id+"F0.wireOp",EDGE,"E238"),sQuery(id+"F0.wireOp",EDGE,"E239"),sQuery(id+"F0.wireOp",EDGE,"E240"),sQuery(id+"F0.wireOp",EDGE,"E241"),sQuery(id+"F0.wireOp",EDGE,"E243"),sQuery(id+"F0.wireOp",EDGE,"E244"),sQuery(id+"F0.wireOp",EDGE,"E245"),sQuery(id+"F0.wireOp",EDGE,"E246"),sQuery(id+"F0.wireOp",EDGE,"E247"),sQuery(id+"F0.wireOp",EDGE,"E248"),sQuery(id+"F0.wireOp",EDGE,"E250"),sQuery(id+"F0.wireOp",EDGE,"E251"),sQuery(id+"F0.wireOp",EDGE,"E252.trimOffspring"),sQuery(id+"F0.wireOp",EDGE,"E253.trimOffspring"),sQuery(id+"F0.wireOp",EDGE,"E254.trimOffspring"),sQuery(id+"F0.wireOp",EDGE,"E255.trimOffspring"),sQuery(id+"F0.wireOp",EDGE,"E256.trimOffspring"),sQuery(id+"F0.wireOp",EDGE,"E257.trimOffspring"),sQuery(id+"F0.wireOp",EDGE,"E258.trimOffspring"),sQuery(id+"F0.wireOp",EDGE,"E259.trimOffspring"),sQuery(id+"F0.wireOp",EDGE,"E260.filletArc"),sQuery(id+"F0.wireOp",EDGE,"E261.filletArc"),sQuery(id+"F0.wireOp",EDGE,"E262.filletArc"),sQuery(id+"F0.wireOp",EDGE,"E263.filletArc"),sQuery(id+"F0.wireOp",EDGE,"E264.filletArc"),sQuery(id+"F0.wireOp",EDGE,"E265.filletArc"),sQuery(id+"F0.wireOp",EDGE,"E266.trimOffspring"),sQuery(id+"F0.wireOp",EDGE,"E267.filletArc"),sQuery(id+"F0.wireOp",EDGE,"E268.filletArc"),sQuery(id+"F0.wireOp",EDGE,"E270.filletArc"),sQuery(id+"F0.wireOp",EDGE,"E271.filletArc"),sQuery(id+"F0.wireOp",EDGE,"E272.filletArc"),sQuery(id+"F0.wireOp",EDGE,"E273.filletArc"),sQuery(id+"F0.wireOp",EDGE,"E274.filletArc"),sQuery(id+"F0.wireOp",EDGE,"E275.filletArc"),sQuery(id+"F0.wireOp",EDGE,"E276.trimOffspring"),sQuery(id+"F0.wireOp",EDGE,"E277.trimOffspring"),sQuery(id+"F0.wireOp",EDGE,"E278.filletArc"),sQuery(id+"F0.wireOp",EDGE,"E280.filletArc"),sQuery(id+"F0.wireOp",EDGE,"E281.filletArc"),sQuery(id+"F0.wireOp",EDGE,"E282.filletArc"),sQuery(id+"F0.wireOp",EDGE,"E283.filletArc"),sQuery(id+"F0.wireOp",EDGE,"E284.filletArc"),sQuery(id+"F0.wireOp",EDGE,"E285.filletArc"),sQuery(id+"F0.wireOp",EDGE,"E286.filletArc"),sQuery(id+"F0.wireOp",EDGE,"E287.filletArc"),sQuery(id+"F0.wireOp",EDGE,"E288.filletArc"),sQuery(id+"F0.wireOp",EDGE,"E289.filletArc"),sQuery(id+"F0.wireOp",EDGE,"E290.filletArc"),sQuery(id+"F0.wireOp",EDGE,"E291.filletArc"),sQuery(id+"F0.wireOp",EDGE,"E292.filletArc")])]});
            hole(context, id + "F4", {"style" : HoleStyle.SIMPLE, "holeDiameter" : 3 * mm, "endStyle" : HoleEndStyle.THROUGH, "locations" : qUnion([Q0, Q1, Q2, Q3, Q4, Q5, Q6, Q7]), "scope" : qUnion([Q8])});
        }
        {
            var Q0;
            Q0=sQuery(id+"F0.wireOp",VERTEX,"E87.MirrorC.center");
            var Q1;
            Q1=sQuery(id+"F0.wireOp",VERTEX,"E83.center");
            var Q2;
            Q2=sQuery(id+"F0.wireOp",VERTEX,"E88.MirrorC.center");
            var Q3;
            Q3=sQuery(id+"F0.wireOp",VERTEX,"E84.center");
            var Q4;
            Q4=makeQuery(id+"F3.opExtrude","SWEPT_BODY",BODY,{"disambiguationData":[OSD([sQuery(id+"F0.wireOp",EDGE,"E219"),sQuery(id+"F0.wireOp",EDGE,"E270.filletArc"),sQuery(id+"F0.wireOp",EDGE,"E271.filletArc"),sQuery(id+"F0.wireOp",EDGE,"E276.trimOffspring"),sQuery(id+"F0.wireOp",EDGE,"E278.filletArc"),sQuery(id+"F2.wireOp",EDGE,"E294"),sQuery(id+"F2.wireOp",EDGE,"E295"),sQuery(id+"F2.wireOp",EDGE,"E296"),sQuery(id+"F2.wireOp",EDGE,"E297"),sQuery(id+"F2.wireOp",EDGE,"E298"),sQuery(id+"F2.wireOp",EDGE,"E299"),sQuery(id+"F2.wireOp",EDGE,"E300"),sQuery(id+"F2.wireOp",EDGE,"E301"),sQuery(id+"F2.wireOp",EDGE,"E303"),sQuery(id+"F2.wireOp",EDGE,"E304.trimOffspring"),sQuery(id+"F2.wireOp",EDGE,"E307.filletArc"),sQuery(id+"F2.wireOp",EDGE,"E308.filletArc"),sQuery(id+"F2.wireOp",EDGE,"E309.filletArc"),sQuery(id+"F2.wireOp",EDGE,"E310.filletArc"),sQuery(id+"F2.wireOp",EDGE,"E311.filletArc"),sQuery(id+"F2.wireOp",EDGE,"E312.filletArc"),sQuery(id+"F2.wireOp",EDGE,"E313"),sQuery(id+"F2.wireOp",EDGE,"E314.MirrorC"),sQuery(id+"F2.wireOp",EDGE,"E315.MirrorC"),sQuery(id+"F2.wireOp",EDGE,"E316.MirrorC"),sQuery(id+"F2.wireOp",EDGE,"E317.MirrorC"),sQuery(id+"F2.wireOp",EDGE,"E318.MirrorC"),sQuery(id+"F2.wireOp",EDGE,"E320"),sQuery(id+"F2.wireOp",EDGE,"E321"),sQuery(id+"F2.wireOp",EDGE,"E322"),sQuery(id+"F2.wireOp",EDGE,"E323"),sQuery(id+"F2.wireOp",EDGE,"E324"),sQuery(id+"F2.wireOp",EDGE,"E325.MirrorC"),sQuery(id+"F2.wireOp",EDGE,"E329"),sQuery(id+"F2.wireOp",EDGE,"E330"),sQuery(id+"F2.wireOp",EDGE,"E331"),sQuery(id+"F2.wireOp",EDGE,"E332")])]});
            hole(context, id + "F5", {"style" : HoleStyle.SIMPLE, "holeDiameter" : 3 * mm, "endStyle" : HoleEndStyle.THROUGH, "locations" : qUnion([Q0, Q1, Q2, Q3]), "scope" : qUnion([Q4])});
        }
        {
            var Q0;
            Q0=sQuery(id+"F0.wireOp",VERTEX,"E84.center");
            var Q1;
            Q1=sQuery(id+"F0.wireOp",VERTEX,"E87.MirrorC.center");
            var Q2;
            Q2=sQuery(id+"F0.wireOp",VERTEX,"E83.center");
            var Q3;
            Q3=sQuery(id+"F0.wireOp",VERTEX,"E88.MirrorC.center");
            var Q4;
            Q4=makeQuery(id+"F3.opExtrude","SWEPT_BODY",BODY,{"disambiguationData":[OSD([sQuery(id+"F0.wireOp",EDGE,"E219"),sQuery(id+"F0.wireOp",EDGE,"E270.filletArc"),sQuery(id+"F0.wireOp",EDGE,"E271.filletArc"),sQuery(id+"F0.wireOp",EDGE,"E276.trimOffspring"),sQuery(id+"F0.wireOp",EDGE,"E278.filletArc"),sQuery(id+"F2.wireOp",EDGE,"E294"),sQuery(id+"F2.wireOp",EDGE,"E295"),sQuery(id+"F2.wireOp",EDGE,"E296"),sQuery(id+"F2.wireOp",EDGE,"E297"),sQuery(id+"F2.wireOp",EDGE,"E298"),sQuery(id+"F2.wireOp",EDGE,"E299"),sQuery(id+"F2.wireOp",EDGE,"E300"),sQuery(id+"F2.wireOp",EDGE,"E301"),sQuery(id+"F2.wireOp",EDGE,"E303"),sQuery(id+"F2.wireOp",EDGE,"E304.trimOffspring"),sQuery(id+"F2.wireOp",EDGE,"E307.filletArc"),sQuery(id+"F2.wireOp",EDGE,"E308.filletArc"),sQuery(id+"F2.wireOp",EDGE,"E309.filletArc"),sQuery(id+"F2.wireOp",EDGE,"E310.filletArc"),sQuery(id+"F2.wireOp",EDGE,"E311.filletArc"),sQuery(id+"F2.wireOp",EDGE,"E312.filletArc"),sQuery(id+"F2.wireOp",EDGE,"E313"),sQuery(id+"F2.wireOp",EDGE,"E314.MirrorC"),sQuery(id+"F2.wireOp",EDGE,"E315.MirrorC"),sQuery(id+"F2.wireOp",EDGE,"E316.MirrorC"),sQuery(id+"F2.wireOp",EDGE,"E317.MirrorC"),sQuery(id+"F2.wireOp",EDGE,"E318.MirrorC"),sQuery(id+"F2.wireOp",EDGE,"E320"),sQuery(id+"F2.wireOp",EDGE,"E321"),sQuery(id+"F2.wireOp",EDGE,"E322"),sQuery(id+"F2.wireOp",EDGE,"E323"),sQuery(id+"F2.wireOp",EDGE,"E324"),sQuery(id+"F2.wireOp",EDGE,"E325.MirrorC"),sQuery(id+"F2.wireOp",EDGE,"E329"),sQuery(id+"F2.wireOp",EDGE,"E330"),sQuery(id+"F2.wireOp",EDGE,"E331"),sQuery(id+"F2.wireOp",EDGE,"E332")])]});
            hole(context, id + "F6", {"style" : HoleStyle.SIMPLE, "holeDiameter" : 3 * mm, "endStyle" : HoleEndStyle.THROUGH, "oppositeDirection" : true, "locations" : qUnion([Q0, Q1, Q2, Q3]), "scope" : qUnion([Q4])});
        }
    });
